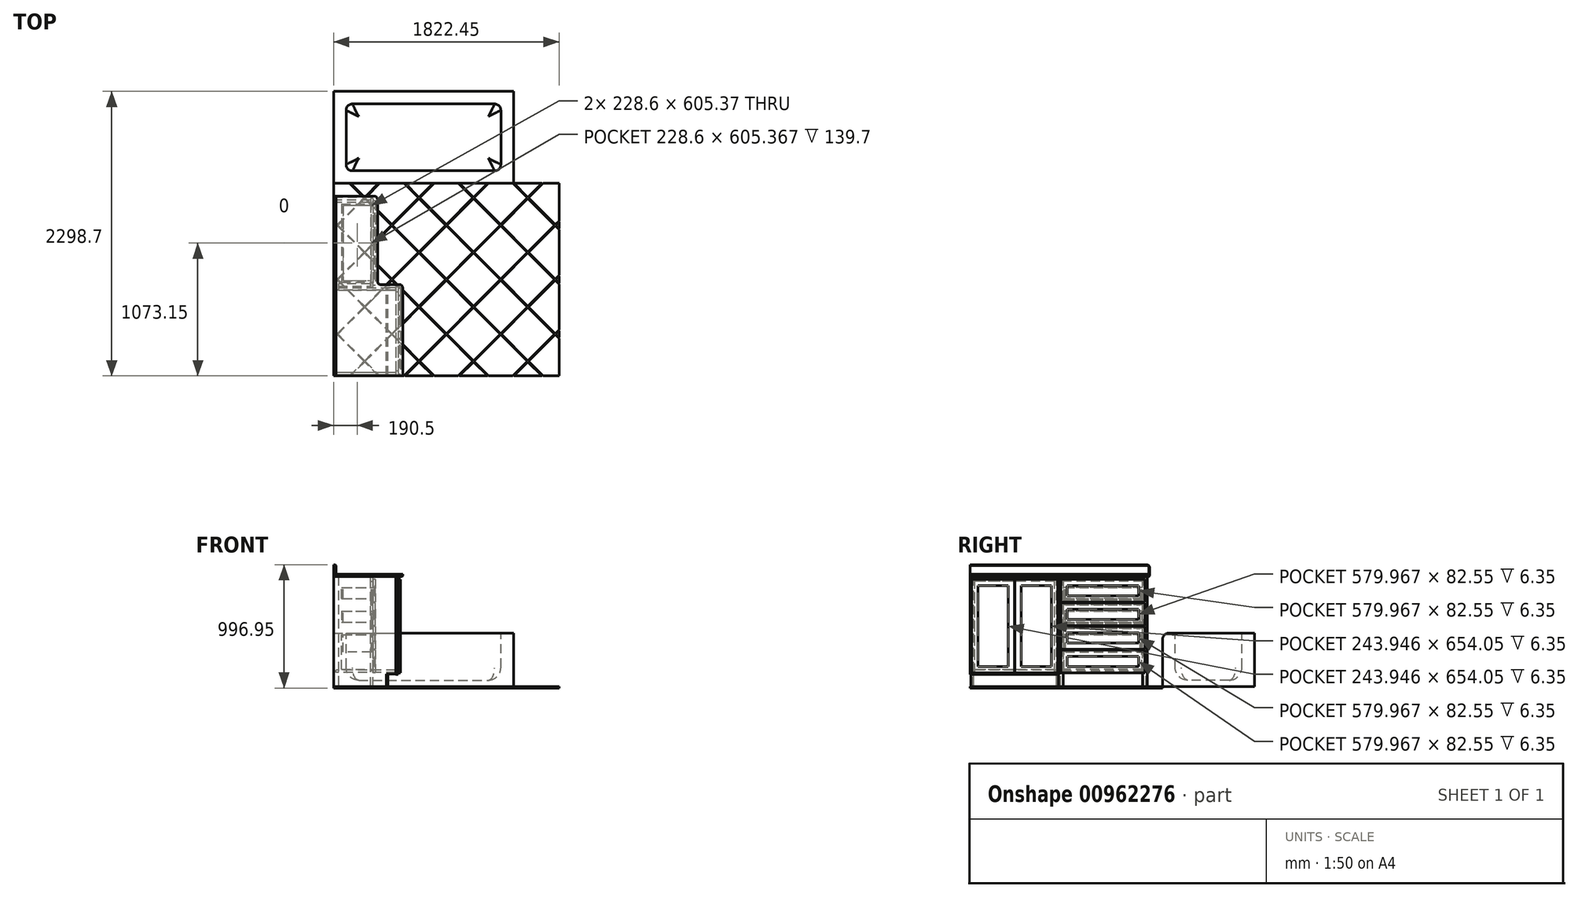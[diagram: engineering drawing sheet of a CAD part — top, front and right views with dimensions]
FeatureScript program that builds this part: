
annotation { "Feature Type Name" : "Feature", "Feature Type Description" : "" }
export const myFeature = defineFeature(function(context is Context, id is Id, definition is map)
    precondition{}
    {
        {
            var Q0;
            Q0=qCreatedBy(makeId("Top.planeOp"),FACE);
            var sketch = newSketch(context, id + "F0", { "sketchPlane" : qUnion([Q0])});
            skLineSegment(sketch, "E0", {"start": v(863.6, 0) * mm, "end": v(1631.95, 0) * mm});
            skLineSegment(sketch, "E1", {"start": v(863.6, 0) * mm, "end": v(0, 0) * mm});
            skLineSegment(sketch, "E2", {"start": v(0, 0) * mm, "end": v(0, 2298.7) * mm});
            skLineSegment(sketch, "E3", {"start": v(0, 2298.7) * mm, "end": v(1454.15, 2298.7) * mm});
            skLineSegment(sketch, "E4", {"start": v(1454.15, 2298.7) * mm, "end": v(1454.15, 1555.75) * mm});
            skLineSegment(sketch, "E5", {"start": v(1454.15, 1555.75) * mm, "end": v(1822.45, 1555.75) * mm});
            skLineSegment(sketch, "E6", {"start": v(1822.45, 1555.75) * mm, "end": v(1822.45, 0) * mm});
            skLineSegment(sketch, "E7", {"start": v(1822.45, 0) * mm, "end": v(1631.95, 0) * mm});
            skLineSegment(sketch, "E8", {"start": v(1454.15, 1555.75) * mm, "end": v(0, 1555.75) * mm, "construction": true});
            skLineSegment(sketch, "E9", {"start": v(1466.85, 1327.15) * mm, "end": v(1466.85, 819.15) * mm, "construction": true});
            skLineSegment(sketch, "E10", {"start": v(1111.25, 1073.15) * mm, "end": v(1822.45, 1073.15) * mm, "construction": true});
            skPoint(sketch, "E11", {"position": v(1466.85, 1073.15) * mm});
            skEllipse(sketch, "E12", {"center": v(1466.85, 1073.15) * mm, "majorRadius": 355.6 * mm, "minorRadius": 254 * mm, "majorAxis": v(1, 0)});
            skSolve(sketch);
        }
        {
            var Q0;
            Q0=qCreatedBy(makeId("Top.planeOp"),FACE);
            var sketch = newSketch(context, id + "F1", { "sketchPlane" : qUnion([Q0])});
            skLineSegment(sketch, "E13", {"start": v(863.6, 0) * mm, "end": v(1631.95, 0) * mm});
            skLineSegment(sketch, "E14", {"start": v(863.6, 0) * mm, "end": v(0, 0) * mm});
            skLineSegment(sketch, "E15", {"start": v(0, 0) * mm, "end": v(0, 2298.7) * mm});
            skLineSegment(sketch, "E16", {"start": v(0, 2298.7) * mm, "end": v(1454.15, 2298.7) * mm});
            skLineSegment(sketch, "E17", {"start": v(1454.15, 2298.7) * mm, "end": v(1454.15, 1555.75) * mm});
            skLineSegment(sketch, "E18", {"start": v(1454.15, 1555.75) * mm, "end": v(1822.45, 1555.75) * mm});
            skLineSegment(sketch, "E19", {"start": v(1822.45, 1555.75) * mm, "end": v(1822.45, 0) * mm});
            skLineSegment(sketch, "E20", {"start": v(1822.45, 0) * mm, "end": v(1631.95, 0) * mm});
            skLineSegment(sketch, "E21", {"start": v(1454.15, 1555.75) * mm, "end": v(0, 1555.75) * mm, "construction": true});
            skLineSegment(sketch, "E22", {"start": v(1466.85, 1327.15) * mm, "end": v(1466.85, 819.15) * mm, "construction": true});
            skLineSegment(sketch, "E23", {"start": v(1111.25, 1073.15) * mm, "end": v(1822.45, 1073.15) * mm, "construction": true});
            skPoint(sketch, "E24", {"position": v(1466.85, 1073.15) * mm});
            skEllipse(sketch, "E25", {"center": v(1466.85, 1073.15) * mm, "majorRadius": 355.6 * mm, "minorRadius": 254 * mm, "majorAxis": v(1, 0)});
            skEllipse(sketch, "E26", {"center": v(330.2, 508) * mm, "majorRadius": 336.55 * mm, "minorRadius": 228.6 * mm, "majorAxis": v(0, -1)});
            skLineSegment(sketch, "E27", {"start": v(330.2, 844.55) * mm, "end": v(330.2, 171.45) * mm, "construction": true});
            skLineSegment(sketch, "E28", {"start": v(558.8, 508) * mm, "end": v(101.6, 508) * mm, "construction": true});
            skLineSegment(sketch, "E29", {"start": v(101.6, 508) * mm, "end": v(0, 508) * mm, "construction": true});
            skLineSegment(sketch, "E30.bottom", {"start": v(63.5, 1403.35) * mm, "end": v(431.8, 1403.35) * mm});
            skLineSegment(sketch, "E30.top", {"start": v(63.5, 996.95) * mm, "end": v(431.8, 996.95) * mm});
            skLineSegment(sketch, "E30.left", {"start": v(63.5, 1403.35) * mm, "end": v(63.5, 996.95) * mm});
            skLineSegment(sketch, "E30.right", {"start": v(431.8, 1403.35) * mm, "end": v(431.8, 996.95) * mm});
            skLineSegment(sketch, "E31", {"start": v(0, 787.4) * mm, "end": v(302.35, 842.04) * mm});
            skLineSegment(sketch, "E32", {"start": v(0, 228.6) * mm, "end": v(302.35, 173.96) * mm});
            skSolve(sketch);
        }
        {
            var Q0;
            Q0=qCreatedBy(makeId("Top.planeOp"),FACE);
            var sketch = newSketch(context, id + "F2", { "sketchPlane" : qUnion([Q0])});
            skLineSegment(sketch, "E33.bottom", {"start": v(520.7, 0) * mm, "end": v(501.65, 0) * mm});
            skLineSegment(sketch, "E33.top", {"start": v(520.7, 38.1) * mm, "end": v(501.65, 38.1) * mm});
            skLineSegment(sketch, "E33.left", {"start": v(520.7, 0) * mm, "end": v(520.7, 38.1) * mm});
            skLineSegment(sketch, "E33.right", {"start": v(501.65, 0) * mm, "end": v(501.65, 38.1) * mm});
            skLineSegment(sketch, "E34.bottom", {"start": v(520.7, 681.57) * mm, "end": v(501.65, 681.57) * mm});
            skLineSegment(sketch, "E34.top", {"start": v(520.7, 719.67) * mm, "end": v(501.65, 719.67) * mm});
            skLineSegment(sketch, "E34.left", {"start": v(520.7, 681.57) * mm, "end": v(520.7, 719.67) * mm});
            skLineSegment(sketch, "E34.right", {"start": v(501.65, 681.57) * mm, "end": v(501.65, 719.67) * mm});
            skLineSegment(sketch, "E35.bottom", {"start": v(317.5, 1394.88) * mm, "end": v(298.45, 1394.88) * mm});
            skLineSegment(sketch, "E35.top", {"start": v(317.5, 1432.98) * mm, "end": v(298.45, 1432.98) * mm});
            skLineSegment(sketch, "E35.left", {"start": v(317.5, 1394.88) * mm, "end": v(317.5, 1432.98) * mm});
            skLineSegment(sketch, "E35.right", {"start": v(298.45, 1394.88) * mm, "end": v(298.45, 1432.98) * mm});
            skLineSegment(sketch, "E36", {"start": v(317.5, 1394.88) * mm, "end": v(317.5, 751.42) * mm});
            skLineSegment(sketch, "E37", {"start": v(298.45, 1394.88) * mm, "end": v(298.45, 751.42) * mm});
            skLineSegment(sketch, "E38.bottom", {"start": v(298.45, 751.42) * mm, "end": v(317.5, 751.42) * mm});
            skLineSegment(sketch, "E38.top", {"start": v(298.45, 713.32) * mm, "end": v(317.5, 713.32) * mm});
            skLineSegment(sketch, "E38.left", {"start": v(298.45, 751.42) * mm, "end": v(298.45, 713.32) * mm});
            skLineSegment(sketch, "E38.right", {"start": v(317.5, 751.42) * mm, "end": v(317.5, 713.32) * mm});
            skLineSegment(sketch, "E39", {"start": v(501.65, 713.32) * mm, "end": v(38.1, 713.32) * mm});
            skLineSegment(sketch, "E40", {"start": v(501.65, 694.27) * mm, "end": v(38.1, 694.27) * mm});
            skLineSegment(sketch, "E41", {"start": v(501.65, 681.57) * mm, "end": v(501.65, 38.1) * mm});
            skLineSegment(sketch, "E42", {"start": v(520.7, 681.57) * mm, "end": v(520.7, 38.1) * mm});
            skLineSegment(sketch, "E43", {"start": v(298.45, 1420.28) * mm, "end": v(0, 1420.28) * mm});
            skLineSegment(sketch, "E44", {"start": v(0, 1420.28) * mm, "end": v(0, 1401.23) * mm});
            skLineSegment(sketch, "E45", {"start": v(0, 1401.23) * mm, "end": v(298.45, 1401.23) * mm});
            skLineSegment(sketch, "E46", {"start": v(0, 1420.28) * mm, "end": v(0, 1426.63) * mm});
            skLineSegment(sketch, "E47", {"start": v(0, 1426.63) * mm, "end": v(298.45, 1426.63) * mm});
            skLineSegment(sketch, "E48", {"start": v(501.65, 6.35) * mm, "end": v(0, 6.35) * mm});
            skLineSegment(sketch, "E49", {"start": v(0, 6.35) * mm, "end": v(0, 25.4) * mm});
            skLineSegment(sketch, "E50", {"start": v(0, 25.4) * mm, "end": v(501.65, 25.4) * mm});
            skLineSegment(sketch, "E51", {"start": v(38.1, 713.32) * mm, "end": v(38.1, 694.27) * mm});
            skLineSegment(sketch, "E52", {"start": v(298.45, 745.07) * mm, "end": v(38.1, 745.07) * mm});
            skLineSegment(sketch, "E53", {"start": v(38.1, 745.07) * mm, "end": v(38.1, 726.02) * mm});
            skLineSegment(sketch, "E54", {"start": v(38.1, 726.02) * mm, "end": v(298.45, 726.02) * mm});
            skLineSegment(sketch, "E55", {"start": v(0, 1394.88) * mm, "end": v(0, 31.75) * mm});
            skLineSegment(sketch, "E56", {"start": v(19.05, 1401.23) * mm, "end": v(19.05, 25.4) * mm});
            skLineSegment(sketch, "E57", {"start": v(38.1, 1401.23) * mm, "end": v(38.1, 25.4) * mm});
            skLineSegment(sketch, "E58", {"start": v(0, 1452.03) * mm, "end": v(355.6, 1452.03) * mm});
            skLineSegment(sketch, "E59", {"start": v(355.6, 1452.03) * mm, "end": v(355.6, 738.72) * mm});
            skLineSegment(sketch, "E60", {"start": v(355.6, 738.72) * mm, "end": v(558.8, 738.72) * mm});
            skLineSegment(sketch, "E61", {"start": v(558.8, 738.72) * mm, "end": v(558.8, 0) * mm});
            skLineSegment(sketch, "E62", {"start": v(558.8, 0) * mm, "end": v(0, 0) * mm});
            skLineSegment(sketch, "E63", {"start": v(0, 0) * mm, "end": v(0, 1452.03) * mm});
            skLineSegment(sketch, "E64", {"start": v(317.5, 1413.93) * mm, "end": v(336.55, 1413.93) * mm, "construction": true});
            skLineSegment(sketch, "E65", {"start": v(336.55, 1413.93) * mm, "end": v(336.55, 732.37) * mm, "construction": true});
            skLineSegment(sketch, "E66", {"start": v(336.55, 732.37) * mm, "end": v(317.5, 732.37) * mm, "construction": true});
            skLineSegment(sketch, "E67", {"start": v(317.5, 1388.53) * mm, "end": v(63.5, 1388.53) * mm, "construction": true});
            skLineSegment(sketch, "E68", {"start": v(63.5, 757.77) * mm, "end": v(317.5, 757.77) * mm, "construction": true});
            skLineSegment(sketch, "E69", {"start": v(63.5, 1388.53) * mm, "end": v(63.5, 1375.83) * mm, "construction": true});
            skLineSegment(sketch, "E70", {"start": v(63.5, 1375.83) * mm, "end": v(76.2, 1375.83) * mm, "construction": true});
            skLineSegment(sketch, "E71", {"start": v(76.2, 770.47) * mm, "end": v(63.5, 770.47) * mm, "construction": true});
            skLineSegment(sketch, "E72", {"start": v(63.5, 770.47) * mm, "end": v(63.5, 757.77) * mm, "construction": true});
            skLineSegment(sketch, "E73", {"start": v(76.2, 1382.18) * mm, "end": v(76.2, 764.12) * mm, "construction": true});
            skLineSegment(sketch, "E74", {"start": v(76.2, 764.12) * mm, "end": v(82.55, 764.12) * mm, "construction": true});
            skLineSegment(sketch, "E75", {"start": v(82.55, 764.12) * mm, "end": v(82.55, 770.47) * mm, "construction": true});
            skLineSegment(sketch, "E76", {"start": v(76.2, 1382.18) * mm, "end": v(82.55, 1382.18) * mm, "construction": true});
            skLineSegment(sketch, "E77", {"start": v(82.55, 1382.18) * mm, "end": v(82.55, 1375.83) * mm, "construction": true});
            skLineSegment(sketch, "E78", {"start": v(88.9, 1375.83) * mm, "end": v(88.9, 770.47) * mm, "construction": true});
            skLineSegment(sketch, "E79", {"start": v(82.55, 1375.83) * mm, "end": v(317.5, 1375.83) * mm, "construction": true});
            skLineSegment(sketch, "E80", {"start": v(82.55, 770.47) * mm, "end": v(317.5, 770.47) * mm, "construction": true});
            skLineSegment(sketch, "E81", {"start": v(317.5, 1073.15) * mm, "end": v(336.55, 1073.15) * mm, "construction": true});
            skLineSegment(sketch, "E82", {"start": v(520.7, 706.97) * mm, "end": v(539.75, 706.97) * mm, "construction": true});
            skLineSegment(sketch, "E83", {"start": v(539.75, 706.97) * mm, "end": v(539.75, 361.42) * mm, "construction": true});
            skLineSegment(sketch, "E84", {"start": v(539.75, 361.42) * mm, "end": v(520.7, 361.42) * mm, "construction": true});
            skLineSegment(sketch, "E85", {"start": v(520.7, 358.25) * mm, "end": v(539.75, 358.25) * mm, "construction": true});
            skLineSegment(sketch, "E86", {"start": v(539.75, 358.25) * mm, "end": v(539.75, 12.7) * mm, "construction": true});
            skLineSegment(sketch, "E87", {"start": v(539.75, 12.7) * mm, "end": v(520.7, 12.7) * mm, "construction": true});
            skLineSegment(sketch, "E88", {"start": v(539.75, 361.42) * mm, "end": v(539.75, 358.25) * mm, "construction": true});
            skLineSegment(sketch, "E89", {"start": v(539.75, 359.83) * mm, "end": v(520.7, 359.83) * mm, "construction": true});
            skLineSegment(sketch, "E90", {"start": v(0, 1394.88) * mm, "end": v(19.05, 1394.88) * mm});
            skLineSegment(sketch, "E91", {"start": v(0, 31.75) * mm, "end": v(19.05, 31.75) * mm});
            skLineSegment(sketch, "E92", {"start": v(76.2, 668.87) * mm, "end": v(76.2, 50.8) * mm, "construction": true});
            skLineSegment(sketch, "E93", {"start": v(63.5, 57.15) * mm, "end": v(63.5, 44.45) * mm, "construction": true});
            skLineSegment(sketch, "E94", {"start": v(63.5, 44.45) * mm, "end": v(539.75, 44.45) * mm, "construction": true});
            skLineSegment(sketch, "E95", {"start": v(76.2, 50.8) * mm, "end": v(82.55, 50.8) * mm, "construction": true});
            skLineSegment(sketch, "E96", {"start": v(82.55, 50.8) * mm, "end": v(82.55, 57.15) * mm, "construction": true});
            skLineSegment(sketch, "E97", {"start": v(88.9, 57.15) * mm, "end": v(88.9, 662.52) * mm, "construction": true});
            skLineSegment(sketch, "E98", {"start": v(82.55, 662.52) * mm, "end": v(82.55, 668.87) * mm, "construction": true});
            skLineSegment(sketch, "E99", {"start": v(82.55, 668.87) * mm, "end": v(76.2, 668.87) * mm, "construction": true});
            skLineSegment(sketch, "E100", {"start": v(76.2, 662.52) * mm, "end": v(63.5, 662.52) * mm, "construction": true});
            skLineSegment(sketch, "E101", {"start": v(63.5, 662.52) * mm, "end": v(63.5, 675.22) * mm, "construction": true});
            skLineSegment(sketch, "E102", {"start": v(63.5, 675.22) * mm, "end": v(539.75, 675.22) * mm, "construction": true});
            skLineSegment(sketch, "E103", {"start": v(82.55, 662.52) * mm, "end": v(539.75, 662.52) * mm, "construction": true});
            skLineSegment(sketch, "E104", {"start": v(63.5, 57.15) * mm, "end": v(76.2, 57.15) * mm, "construction": true});
            skLineSegment(sketch, "E105", {"start": v(82.55, 57.15) * mm, "end": v(539.75, 57.15) * mm, "construction": true});
            skLineSegment(sketch, "E106", {"start": v(1466.85, 1073.15) * mm, "end": v(336.55, 1073.15) * mm, "construction": true});
            skSolve(sketch);
        }
        {
            var Q0;
            Q0=qCreatedBy(makeId("Top.planeOp"),FACE);
            var sketch = newSketch(context, id + "F3", { "sketchPlane" : qUnion([Q0])});
            skLineSegment(sketch, "E107", {"start": v(695.7, -762.24) * mm, "end": v(911.23, -977.77) * mm});
            skLineSegment(sketch, "E108", {"start": v(911.23, -977.77) * mm, "end": v(1126.75, -762.24) * mm});
            skLineSegment(sketch, "E109", {"start": v(1126.75, -762.24) * mm, "end": v(911.23, -546.71) * mm});
            skLineSegment(sketch, "E110", {"start": v(911.23, -546.71) * mm, "end": v(695.7, -762.24) * mm});
            skLineSegment(sketch, "E111.0.1.0", {"start": v(475.68, -542.22) * mm, "end": v(691.2, -757.75) * mm});
            skLineSegment(sketch, "E111.0.1.1", {"start": v(906.73, -542.22) * mm, "end": v(691.2, -326.7) * mm});
            skLineSegment(sketch, "E111.0.1.2", {"start": v(691.2, -326.7) * mm, "end": v(475.68, -542.22) * mm});
            skLineSegment(sketch, "E111.0.1.3", {"start": v(691.2, -757.75) * mm, "end": v(906.73, -542.22) * mm});
            skLineSegment(sketch, "E111.1.0.0", {"start": v(915.72, -542.22) * mm, "end": v(1131.24, -757.75) * mm});
            skLineSegment(sketch, "E111.1.0.1", {"start": v(1346.77, -542.22) * mm, "end": v(1131.24, -326.7) * mm});
            skLineSegment(sketch, "E111.1.0.2", {"start": v(1131.24, -326.7) * mm, "end": v(915.72, -542.22) * mm});
            skLineSegment(sketch, "E111.1.0.3", {"start": v(1131.24, -757.75) * mm, "end": v(1346.77, -542.22) * mm});
            skLineSegment(sketch, "E111.1.1.0", {"start": v(695.7, -322.2) * mm, "end": v(911.23, -537.73) * mm});
            skLineSegment(sketch, "E111.1.1.1", {"start": v(1126.75, -322.2) * mm, "end": v(911.23, -106.68) * mm});
            skLineSegment(sketch, "E111.1.1.2", {"start": v(911.23, -106.68) * mm, "end": v(695.7, -322.2) * mm});
            skLineSegment(sketch, "E111.1.1.3", {"start": v(911.23, -537.73) * mm, "end": v(1126.75, -322.2) * mm});
            skLineSegment(sketch, "E111.2.0.0", {"start": v(1135.73, -322.2) * mm, "end": v(1351.26, -537.73) * mm});
            skLineSegment(sketch, "E111.2.0.1", {"start": v(1566.78, -322.2) * mm, "end": v(1351.26, -106.68) * mm});
            skLineSegment(sketch, "E111.2.0.2", {"start": v(1351.26, -106.68) * mm, "end": v(1135.73, -322.2) * mm});
            skLineSegment(sketch, "E111.2.0.3", {"start": v(1351.26, -537.73) * mm, "end": v(1566.78, -322.2) * mm});
            skLineSegment(sketch, "E111.2.1.0", {"start": v(915.72, -102.2) * mm, "end": v(1131.24, -317.72) * mm});
            skLineSegment(sketch, "E111.2.1.1", {"start": v(1346.77, -102.2) * mm, "end": v(1131.24, 113.34) * mm});
            skLineSegment(sketch, "E111.2.1.2", {"start": v(1131.24, 113.34) * mm, "end": v(915.72, -102.2) * mm});
            skLineSegment(sketch, "E111.2.1.3", {"start": v(1131.24, -317.72) * mm, "end": v(1346.77, -102.2) * mm});
            skLineSegment(sketch, "E111.direction1", {"start": v(911.22, -977.77) * mm, "end": v(1131.24, -757.75) * mm, "construction": true});
            skLineSegment(sketch, "E111.direction2", {"start": v(911.23, -977.77) * mm, "end": v(691.2, -757.75) * mm, "construction": true});
            skLineSegment(sketch, "E112.0.3.0", {"start": v(1355.75, -102.2) * mm, "end": v(1571.27, -317.72) * mm});
            skLineSegment(sketch, "E112.3.3.0", {"start": v(1786.8, -102.2) * mm, "end": v(1571.27, 113.34) * mm});
            skLineSegment(sketch, "E112.6.3.0", {"start": v(1571.27, 113.34) * mm, "end": v(1355.75, -102.2) * mm});
            skLineSegment(sketch, "E112.9.3.0", {"start": v(1571.27, -317.72) * mm, "end": v(1786.8, -102.2) * mm});
            skLineSegment(sketch, "E112.0.3.1", {"start": v(1135.73, 117.83) * mm, "end": v(1351.26, -97.7) * mm});
            skLineSegment(sketch, "E112.3.3.1", {"start": v(1566.78, 117.83) * mm, "end": v(1351.26, 333.35) * mm});
            skLineSegment(sketch, "E112.6.3.1", {"start": v(1351.26, 333.35) * mm, "end": v(1135.73, 117.83) * mm});
            skLineSegment(sketch, "E112.9.3.1", {"start": v(1351.26, -97.7) * mm, "end": v(1566.78, 117.83) * mm});
            skLineSegment(sketch, "E112.0.4.0", {"start": v(1575.76, 117.83) * mm, "end": v(1791.3, -97.7) * mm});
            skLineSegment(sketch, "E112.3.4.0", {"start": v(2006.82, 117.83) * mm, "end": v(1791.3, 333.35) * mm});
            skLineSegment(sketch, "E112.6.4.0", {"start": v(1791.3, 333.35) * mm, "end": v(1575.76, 117.83) * mm});
            skLineSegment(sketch, "E112.9.4.0", {"start": v(1791.3, -97.7) * mm, "end": v(2006.82, 117.83) * mm});
            skLineSegment(sketch, "E112.0.4.1", {"start": v(1355.75, 337.84) * mm, "end": v(1571.27, 122.32) * mm});
            skLineSegment(sketch, "E112.3.4.1", {"start": v(1786.8, 337.84) * mm, "end": v(1571.27, 553.37) * mm});
            skLineSegment(sketch, "E112.6.4.1", {"start": v(1571.27, 553.37) * mm, "end": v(1355.75, 337.84) * mm});
            skLineSegment(sketch, "E112.9.4.1", {"start": v(1571.27, 122.32) * mm, "end": v(1786.8, 337.84) * mm});
            skLineSegment(sketch, "E113.0.0.2", {"start": v(255.67, -322.2) * mm, "end": v(471.2, -537.73) * mm});
            skLineSegment(sketch, "E113.3.0.2", {"start": v(686.72, -322.2) * mm, "end": v(471.2, -106.68) * mm});
            skLineSegment(sketch, "E113.6.0.2", {"start": v(471.2, -106.68) * mm, "end": v(255.67, -322.2) * mm});
            skLineSegment(sketch, "E113.9.0.2", {"start": v(471.2, -537.73) * mm, "end": v(686.72, -322.2) * mm});
            skLineSegment(sketch, "E113.0.0.3", {"start": v(35.65, -102.2) * mm, "end": v(251.18, -317.72) * mm});
            skLineSegment(sketch, "E113.3.0.3", {"start": v(466.7, -102.2) * mm, "end": v(251.18, 113.34) * mm});
            skLineSegment(sketch, "E113.6.0.3", {"start": v(251.18, 113.34) * mm, "end": v(35.65, -102.2) * mm});
            skLineSegment(sketch, "E113.9.0.3", {"start": v(251.18, -317.72) * mm, "end": v(466.7, -102.2) * mm});
            skLineSegment(sketch, "E113.0.0.4", {"start": v(-184.37, 117.83) * mm, "end": v(31.16, -97.7) * mm});
            skLineSegment(sketch, "E113.3.0.4", {"start": v(246.69, 117.83) * mm, "end": v(31.16, 333.35) * mm});
            skLineSegment(sketch, "E113.6.0.4", {"start": v(31.16, 333.35) * mm, "end": v(-184.37, 117.83) * mm});
            skLineSegment(sketch, "E113.9.0.4", {"start": v(31.16, -97.7) * mm, "end": v(246.69, 117.83) * mm});
            skLineSegment(sketch, "E113.0.1.2", {"start": v(475.68, -102.2) * mm, "end": v(691.2, -317.72) * mm});
            skLineSegment(sketch, "E113.3.1.2", {"start": v(906.73, -102.2) * mm, "end": v(691.2, 113.34) * mm});
            skLineSegment(sketch, "E113.6.1.2", {"start": v(691.2, 113.34) * mm, "end": v(475.68, -102.2) * mm});
            skLineSegment(sketch, "E113.9.1.2", {"start": v(691.2, -317.72) * mm, "end": v(906.73, -102.2) * mm});
            skLineSegment(sketch, "E113.0.1.3", {"start": v(255.67, 117.83) * mm, "end": v(471.2, -97.7) * mm});
            skLineSegment(sketch, "E113.3.1.3", {"start": v(686.72, 117.83) * mm, "end": v(471.2, 333.35) * mm});
            skLineSegment(sketch, "E113.6.1.3", {"start": v(471.2, 333.35) * mm, "end": v(255.67, 117.83) * mm});
            skLineSegment(sketch, "E113.9.1.3", {"start": v(471.2, -97.7) * mm, "end": v(686.72, 117.83) * mm});
            skLineSegment(sketch, "E113.0.1.4", {"start": v(35.65, 337.84) * mm, "end": v(251.18, 122.32) * mm});
            skLineSegment(sketch, "E113.3.1.4", {"start": v(466.7, 337.84) * mm, "end": v(251.18, 553.37) * mm});
            skLineSegment(sketch, "E113.6.1.4", {"start": v(251.18, 553.37) * mm, "end": v(35.65, 337.84) * mm});
            skLineSegment(sketch, "E113.9.1.4", {"start": v(251.18, 122.32) * mm, "end": v(466.7, 337.84) * mm});
            skLineSegment(sketch, "E113.0.2.2", {"start": v(695.7, 117.83) * mm, "end": v(911.23, -97.7) * mm});
            skLineSegment(sketch, "E113.3.2.2", {"start": v(1126.75, 117.83) * mm, "end": v(911.23, 333.35) * mm});
            skLineSegment(sketch, "E113.6.2.2", {"start": v(911.23, 333.35) * mm, "end": v(695.7, 117.83) * mm});
            skLineSegment(sketch, "E113.9.2.2", {"start": v(911.23, -97.7) * mm, "end": v(1126.75, 117.83) * mm});
            skLineSegment(sketch, "E113.0.2.3", {"start": v(475.68, 337.84) * mm, "end": v(691.2, 122.32) * mm});
            skLineSegment(sketch, "E113.3.2.3", {"start": v(906.73, 337.84) * mm, "end": v(691.2, 553.37) * mm});
            skLineSegment(sketch, "E113.6.2.3", {"start": v(691.2, 553.37) * mm, "end": v(475.68, 337.84) * mm});
            skLineSegment(sketch, "E113.9.2.3", {"start": v(691.2, 122.32) * mm, "end": v(906.73, 337.84) * mm});
            skLineSegment(sketch, "E113.0.2.4", {"start": v(255.67, 557.86) * mm, "end": v(471.2, 342.33) * mm});
            skLineSegment(sketch, "E113.3.2.4", {"start": v(686.72, 557.86) * mm, "end": v(471.2, 773.38) * mm});
            skLineSegment(sketch, "E113.6.2.4", {"start": v(471.2, 773.38) * mm, "end": v(255.67, 557.86) * mm});
            skLineSegment(sketch, "E113.9.2.4", {"start": v(471.2, 342.33) * mm, "end": v(686.72, 557.86) * mm});
            skLineSegment(sketch, "E113.0.3.2", {"start": v(915.72, 337.84) * mm, "end": v(1131.24, 122.32) * mm});
            skLineSegment(sketch, "E113.3.3.2", {"start": v(1346.77, 337.84) * mm, "end": v(1131.24, 553.37) * mm});
            skLineSegment(sketch, "E113.6.3.2", {"start": v(1131.24, 553.37) * mm, "end": v(915.72, 337.84) * mm});
            skLineSegment(sketch, "E113.9.3.2", {"start": v(1131.24, 122.32) * mm, "end": v(1346.77, 337.84) * mm});
            skLineSegment(sketch, "E113.0.3.3", {"start": v(695.7, 557.86) * mm, "end": v(911.23, 342.33) * mm});
            skLineSegment(sketch, "E113.3.3.3", {"start": v(1126.75, 557.86) * mm, "end": v(911.23, 773.38) * mm});
            skLineSegment(sketch, "E113.6.3.3", {"start": v(911.22, 773.38) * mm, "end": v(695.7, 557.86) * mm});
            skLineSegment(sketch, "E113.9.3.3", {"start": v(911.23, 342.33) * mm, "end": v(1126.75, 557.86) * mm});
            skLineSegment(sketch, "E113.0.3.4", {"start": v(475.68, 777.88) * mm, "end": v(691.2, 562.35) * mm});
            skLineSegment(sketch, "E113.3.3.4", {"start": v(906.73, 777.88) * mm, "end": v(691.2, 993.4) * mm});
            skLineSegment(sketch, "E113.6.3.4", {"start": v(691.2, 993.4) * mm, "end": v(475.68, 777.88) * mm});
            skLineSegment(sketch, "E113.9.3.4", {"start": v(691.2, 562.35) * mm, "end": v(906.73, 777.88) * mm});
            skLineSegment(sketch, "E113.0.4.2", {"start": v(1135.73, 557.86) * mm, "end": v(1351.26, 342.33) * mm});
            skLineSegment(sketch, "E113.3.4.2", {"start": v(1566.78, 557.86) * mm, "end": v(1351.26, 773.38) * mm});
            skLineSegment(sketch, "E113.6.4.2", {"start": v(1351.26, 773.38) * mm, "end": v(1135.73, 557.86) * mm});
            skLineSegment(sketch, "E113.9.4.2", {"start": v(1351.26, 342.33) * mm, "end": v(1566.78, 557.86) * mm});
            skLineSegment(sketch, "E113.0.4.3", {"start": v(915.72, 777.88) * mm, "end": v(1131.24, 562.35) * mm});
            skLineSegment(sketch, "E113.3.4.3", {"start": v(1346.77, 777.88) * mm, "end": v(1131.24, 993.4) * mm});
            skLineSegment(sketch, "E113.6.4.3", {"start": v(1131.24, 993.4) * mm, "end": v(915.72, 777.88) * mm});
            skLineSegment(sketch, "E113.9.4.3", {"start": v(1131.24, 562.35) * mm, "end": v(1346.77, 777.88) * mm});
            skLineSegment(sketch, "E113.0.4.4", {"start": v(695.7, 997.9) * mm, "end": v(911.23, 782.37) * mm});
            skLineSegment(sketch, "E113.3.4.4", {"start": v(1126.75, 997.9) * mm, "end": v(911.23, 1213.42) * mm});
            skLineSegment(sketch, "E113.6.4.4", {"start": v(911.22, 1213.42) * mm, "end": v(695.7, 997.9) * mm});
            skLineSegment(sketch, "E113.9.4.4", {"start": v(911.22, 782.37) * mm, "end": v(1126.75, 997.9) * mm});
            skLineSegment(sketch, "E114.0.5.0", {"start": v(1795.78, 337.84) * mm, "end": v(2011.3, 122.32) * mm});
            skLineSegment(sketch, "E114.3.5.0", {"start": v(2226.83, 337.84) * mm, "end": v(2011.3, 553.37) * mm});
            skLineSegment(sketch, "E114.6.5.0", {"start": v(2011.3, 553.37) * mm, "end": v(1795.78, 337.84) * mm});
            skLineSegment(sketch, "E114.9.5.0", {"start": v(2011.3, 122.32) * mm, "end": v(2226.83, 337.84) * mm});
            skLineSegment(sketch, "E114.0.5.1", {"start": v(1575.76, 557.86) * mm, "end": v(1791.3, 342.33) * mm});
            skLineSegment(sketch, "E114.3.5.1", {"start": v(2006.82, 557.86) * mm, "end": v(1791.3, 773.38) * mm});
            skLineSegment(sketch, "E114.6.5.1", {"start": v(1791.3, 773.38) * mm, "end": v(1575.76, 557.86) * mm});
            skLineSegment(sketch, "E114.9.5.1", {"start": v(1791.3, 342.33) * mm, "end": v(2006.82, 557.86) * mm});
            skLineSegment(sketch, "E114.0.5.2", {"start": v(1355.75, 777.88) * mm, "end": v(1571.27, 562.35) * mm});
            skLineSegment(sketch, "E114.3.5.2", {"start": v(1786.8, 777.88) * mm, "end": v(1571.27, 993.4) * mm});
            skLineSegment(sketch, "E114.6.5.2", {"start": v(1571.27, 993.4) * mm, "end": v(1355.75, 777.88) * mm});
            skLineSegment(sketch, "E114.9.5.2", {"start": v(1571.27, 562.35) * mm, "end": v(1786.8, 777.88) * mm});
            skLineSegment(sketch, "E114.0.5.3", {"start": v(1135.73, 997.9) * mm, "end": v(1351.26, 782.37) * mm});
            skLineSegment(sketch, "E114.3.5.3", {"start": v(1566.78, 997.9) * mm, "end": v(1351.26, 1213.42) * mm});
            skLineSegment(sketch, "E114.6.5.3", {"start": v(1351.26, 1213.42) * mm, "end": v(1135.73, 997.9) * mm});
            skLineSegment(sketch, "E114.9.5.3", {"start": v(1351.26, 782.37) * mm, "end": v(1566.78, 997.9) * mm});
            skLineSegment(sketch, "E114.0.5.4", {"start": v(915.72, 1217.9) * mm, "end": v(1131.24, 1002.38) * mm});
            skLineSegment(sketch, "E114.3.5.4", {"start": v(1346.77, 1217.9) * mm, "end": v(1131.24, 1433.43) * mm});
            skLineSegment(sketch, "E114.6.5.4", {"start": v(1131.24, 1433.43) * mm, "end": v(915.72, 1217.9) * mm});
            skLineSegment(sketch, "E114.9.5.4", {"start": v(1131.24, 1002.38) * mm, "end": v(1346.77, 1217.9) * mm});
            skLineSegment(sketch, "E114.0.6.0", {"start": v(2015.8, 557.86) * mm, "end": v(2231.32, 342.33) * mm});
            skLineSegment(sketch, "E114.3.6.0", {"start": v(2446.85, 557.86) * mm, "end": v(2231.32, 773.38) * mm});
            skLineSegment(sketch, "E114.6.6.0", {"start": v(2231.32, 773.38) * mm, "end": v(2015.8, 557.86) * mm});
            skLineSegment(sketch, "E114.9.6.0", {"start": v(2231.32, 342.33) * mm, "end": v(2446.85, 557.86) * mm});
            skLineSegment(sketch, "E114.0.6.1", {"start": v(1795.78, 777.88) * mm, "end": v(2011.3, 562.35) * mm});
            skLineSegment(sketch, "E114.3.6.1", {"start": v(2226.83, 777.88) * mm, "end": v(2011.3, 993.4) * mm});
            skLineSegment(sketch, "E114.6.6.1", {"start": v(2011.3, 993.4) * mm, "end": v(1795.78, 777.88) * mm});
            skLineSegment(sketch, "E114.9.6.1", {"start": v(2011.3, 562.35) * mm, "end": v(2226.83, 777.88) * mm});
            skLineSegment(sketch, "E114.0.6.2", {"start": v(1575.76, 997.9) * mm, "end": v(1791.3, 782.37) * mm});
            skLineSegment(sketch, "E114.3.6.2", {"start": v(2006.82, 997.9) * mm, "end": v(1791.3, 1213.42) * mm});
            skLineSegment(sketch, "E114.6.6.2", {"start": v(1791.3, 1213.42) * mm, "end": v(1575.76, 997.9) * mm});
            skLineSegment(sketch, "E114.9.6.2", {"start": v(1791.3, 782.37) * mm, "end": v(2006.82, 997.9) * mm});
            skLineSegment(sketch, "E114.0.6.3", {"start": v(1355.75, 1217.9) * mm, "end": v(1571.27, 1002.38) * mm});
            skLineSegment(sketch, "E114.3.6.3", {"start": v(1786.8, 1217.9) * mm, "end": v(1571.27, 1433.43) * mm});
            skLineSegment(sketch, "E114.6.6.3", {"start": v(1571.27, 1433.43) * mm, "end": v(1355.75, 1217.9) * mm});
            skLineSegment(sketch, "E114.9.6.3", {"start": v(1571.27, 1002.38) * mm, "end": v(1786.8, 1217.9) * mm});
            skLineSegment(sketch, "E114.0.6.4", {"start": v(1135.73, 1437.92) * mm, "end": v(1351.26, 1222.4) * mm});
            skLineSegment(sketch, "E114.3.6.4", {"start": v(1566.78, 1437.92) * mm, "end": v(1351.26, 1653.45) * mm});
            skLineSegment(sketch, "E114.6.6.4", {"start": v(1351.26, 1653.45) * mm, "end": v(1135.73, 1437.92) * mm});
            skLineSegment(sketch, "E114.9.6.4", {"start": v(1351.26, 1222.4) * mm, "end": v(1566.78, 1437.92) * mm});
            skLineSegment(sketch, "E115.0.0.5", {"start": v(-404.38, 337.84) * mm, "end": v(-188.86, 122.32) * mm});
            skLineSegment(sketch, "E115.3.0.5", {"start": v(26.67, 337.84) * mm, "end": v(-188.86, 553.37) * mm});
            skLineSegment(sketch, "E115.6.0.5", {"start": v(-188.86, 553.37) * mm, "end": v(-404.38, 337.84) * mm});
            skLineSegment(sketch, "E115.9.0.5", {"start": v(-188.86, 122.32) * mm, "end": v(26.67, 337.84) * mm});
            skLineSegment(sketch, "E115.0.0.6", {"start": v(-624.4, 557.86) * mm, "end": v(-408.87, 342.33) * mm});
            skLineSegment(sketch, "E115.3.0.6", {"start": v(-193.35, 557.86) * mm, "end": v(-408.87, 773.38) * mm});
            skLineSegment(sketch, "E115.6.0.6", {"start": v(-408.87, 773.38) * mm, "end": v(-624.4, 557.86) * mm});
            skLineSegment(sketch, "E115.9.0.6", {"start": v(-408.87, 342.33) * mm, "end": v(-193.35, 557.86) * mm});
            skLineSegment(sketch, "E115.0.1.5", {"start": v(-184.37, 557.86) * mm, "end": v(31.16, 342.33) * mm});
            skLineSegment(sketch, "E115.3.1.5", {"start": v(246.69, 557.86) * mm, "end": v(31.16, 773.38) * mm});
            skLineSegment(sketch, "E115.6.1.5", {"start": v(31.16, 773.38) * mm, "end": v(-184.37, 557.86) * mm});
            skLineSegment(sketch, "E115.9.1.5", {"start": v(31.16, 342.33) * mm, "end": v(246.69, 557.86) * mm});
            skLineSegment(sketch, "E115.0.1.6", {"start": v(-404.38, 777.88) * mm, "end": v(-188.86, 562.35) * mm});
            skLineSegment(sketch, "E115.3.1.6", {"start": v(26.67, 777.88) * mm, "end": v(-188.86, 993.4) * mm});
            skLineSegment(sketch, "E115.6.1.6", {"start": v(-188.86, 993.4) * mm, "end": v(-404.38, 777.88) * mm});
            skLineSegment(sketch, "E115.9.1.6", {"start": v(-188.86, 562.35) * mm, "end": v(26.67, 777.88) * mm});
            skLineSegment(sketch, "E115.0.2.5", {"start": v(35.65, 777.88) * mm, "end": v(251.18, 562.35) * mm});
            skLineSegment(sketch, "E115.3.2.5", {"start": v(466.7, 777.88) * mm, "end": v(251.18, 993.4) * mm});
            skLineSegment(sketch, "E115.6.2.5", {"start": v(251.18, 993.4) * mm, "end": v(35.65, 777.88) * mm});
            skLineSegment(sketch, "E115.9.2.5", {"start": v(251.18, 562.35) * mm, "end": v(466.7, 777.88) * mm});
            skLineSegment(sketch, "E115.0.2.6", {"start": v(-184.37, 997.9) * mm, "end": v(31.16, 782.37) * mm});
            skLineSegment(sketch, "E115.3.2.6", {"start": v(246.69, 997.9) * mm, "end": v(31.16, 1213.42) * mm});
            skLineSegment(sketch, "E115.6.2.6", {"start": v(31.16, 1213.42) * mm, "end": v(-184.37, 997.9) * mm});
            skLineSegment(sketch, "E115.9.2.6", {"start": v(31.16, 782.37) * mm, "end": v(246.69, 997.9) * mm});
            skLineSegment(sketch, "E115.0.3.5", {"start": v(255.67, 997.9) * mm, "end": v(471.2, 782.37) * mm});
            skLineSegment(sketch, "E115.3.3.5", {"start": v(686.72, 997.9) * mm, "end": v(471.2, 1213.42) * mm});
            skLineSegment(sketch, "E115.6.3.5", {"start": v(471.2, 1213.42) * mm, "end": v(255.67, 997.9) * mm});
            skLineSegment(sketch, "E115.9.3.5", {"start": v(471.2, 782.37) * mm, "end": v(686.72, 997.9) * mm});
            skLineSegment(sketch, "E115.0.3.6", {"start": v(35.65, 1217.9) * mm, "end": v(251.18, 1002.38) * mm});
            skLineSegment(sketch, "E115.3.3.6", {"start": v(466.7, 1217.9) * mm, "end": v(251.18, 1433.43) * mm});
            skLineSegment(sketch, "E115.6.3.6", {"start": v(251.18, 1433.43) * mm, "end": v(35.65, 1217.9) * mm});
            skLineSegment(sketch, "E115.9.3.6", {"start": v(251.18, 1002.38) * mm, "end": v(466.7, 1217.9) * mm});
            skLineSegment(sketch, "E115.0.4.5", {"start": v(475.68, 1217.9) * mm, "end": v(691.2, 1002.38) * mm});
            skLineSegment(sketch, "E115.3.4.5", {"start": v(906.73, 1217.9) * mm, "end": v(691.2, 1433.43) * mm});
            skLineSegment(sketch, "E115.6.4.5", {"start": v(691.2, 1433.43) * mm, "end": v(475.68, 1217.9) * mm});
            skLineSegment(sketch, "E115.9.4.5", {"start": v(691.2, 1002.38) * mm, "end": v(906.73, 1217.9) * mm});
            skLineSegment(sketch, "E115.0.4.6", {"start": v(255.67, 1437.92) * mm, "end": v(471.2, 1222.4) * mm});
            skLineSegment(sketch, "E115.3.4.6", {"start": v(686.72, 1437.92) * mm, "end": v(471.2, 1653.45) * mm});
            skLineSegment(sketch, "E115.6.4.6", {"start": v(471.2, 1653.45) * mm, "end": v(255.67, 1437.92) * mm});
            skLineSegment(sketch, "E115.9.4.6", {"start": v(471.2, 1222.4) * mm, "end": v(686.72, 1437.92) * mm});
            skLineSegment(sketch, "E115.0.5.5", {"start": v(695.7, 1437.92) * mm, "end": v(911.23, 1222.4) * mm});
            skLineSegment(sketch, "E115.3.5.5", {"start": v(1126.75, 1437.92) * mm, "end": v(911.22, 1653.45) * mm});
            skLineSegment(sketch, "E115.6.5.5", {"start": v(911.22, 1653.45) * mm, "end": v(695.7, 1437.92) * mm});
            skLineSegment(sketch, "E115.9.5.5", {"start": v(911.23, 1222.4) * mm, "end": v(1126.75, 1437.92) * mm});
            skLineSegment(sketch, "E115.0.5.6", {"start": v(475.68, 1657.94) * mm, "end": v(691.2, 1442.41) * mm});
            skLineSegment(sketch, "E115.3.5.6", {"start": v(906.73, 1657.94) * mm, "end": v(691.2, 1873.47) * mm});
            skLineSegment(sketch, "E115.6.5.6", {"start": v(691.2, 1873.47) * mm, "end": v(475.68, 1657.94) * mm});
            skLineSegment(sketch, "E115.9.5.6", {"start": v(691.2, 1442.41) * mm, "end": v(906.73, 1657.94) * mm});
            skLineSegment(sketch, "E115.0.6.5", {"start": v(915.72, 1657.94) * mm, "end": v(1131.24, 1442.41) * mm});
            skLineSegment(sketch, "E115.3.6.5", {"start": v(1346.77, 1657.94) * mm, "end": v(1131.24, 1873.47) * mm});
            skLineSegment(sketch, "E115.6.6.5", {"start": v(1131.24, 1873.47) * mm, "end": v(915.72, 1657.94) * mm});
            skLineSegment(sketch, "E115.9.6.5", {"start": v(1131.24, 1442.41) * mm, "end": v(1346.77, 1657.94) * mm});
            skLineSegment(sketch, "E115.0.6.6", {"start": v(695.7, 1877.96) * mm, "end": v(911.22, 1662.43) * mm});
            skLineSegment(sketch, "E115.3.6.6", {"start": v(1126.75, 1877.96) * mm, "end": v(911.22, 2093.48) * mm});
            skLineSegment(sketch, "E115.6.6.6", {"start": v(911.22, 2093.48) * mm, "end": v(695.7, 1877.96) * mm});
            skLineSegment(sketch, "E115.9.6.6", {"start": v(911.22, 1662.43) * mm, "end": v(1126.75, 1877.96) * mm});
            skLineSegment(sketch, "E116.0.0.7", {"start": v(-844.42, 777.88) * mm, "end": v(-628.89, 562.35) * mm});
            skLineSegment(sketch, "E116.3.0.7", {"start": v(-413.36, 777.88) * mm, "end": v(-628.89, 993.4) * mm});
            skLineSegment(sketch, "E116.6.0.7", {"start": v(-628.89, 993.4) * mm, "end": v(-844.42, 777.87) * mm});
            skLineSegment(sketch, "E116.9.0.7", {"start": v(-628.89, 562.35) * mm, "end": v(-413.36, 777.88) * mm});
            skLineSegment(sketch, "E116.0.1.7", {"start": v(-624.4, 997.9) * mm, "end": v(-408.87, 782.37) * mm});
            skLineSegment(sketch, "E116.3.1.7", {"start": v(-193.35, 997.9) * mm, "end": v(-408.87, 1213.42) * mm});
            skLineSegment(sketch, "E116.6.1.7", {"start": v(-408.87, 1213.42) * mm, "end": v(-624.4, 997.9) * mm});
            skLineSegment(sketch, "E116.9.1.7", {"start": v(-408.87, 782.37) * mm, "end": v(-193.35, 997.9) * mm});
            skLineSegment(sketch, "E116.0.2.7", {"start": v(-404.38, 1217.9) * mm, "end": v(-188.86, 1002.38) * mm});
            skLineSegment(sketch, "E116.3.2.7", {"start": v(26.67, 1217.9) * mm, "end": v(-188.86, 1433.43) * mm});
            skLineSegment(sketch, "E116.6.2.7", {"start": v(-188.86, 1433.43) * mm, "end": v(-404.38, 1217.9) * mm});
            skLineSegment(sketch, "E116.9.2.7", {"start": v(-188.86, 1002.38) * mm, "end": v(26.67, 1217.9) * mm});
            skLineSegment(sketch, "E116.0.3.7", {"start": v(-184.37, 1437.92) * mm, "end": v(31.16, 1222.4) * mm});
            skLineSegment(sketch, "E116.3.3.7", {"start": v(246.69, 1437.92) * mm, "end": v(31.16, 1653.45) * mm});
            skLineSegment(sketch, "E116.6.3.7", {"start": v(31.16, 1653.45) * mm, "end": v(-184.37, 1437.92) * mm});
            skLineSegment(sketch, "E116.9.3.7", {"start": v(31.16, 1222.4) * mm, "end": v(246.69, 1437.92) * mm});
            skLineSegment(sketch, "E116.0.4.7", {"start": v(35.65, 1657.94) * mm, "end": v(251.18, 1442.41) * mm});
            skLineSegment(sketch, "E116.3.4.7", {"start": v(466.7, 1657.94) * mm, "end": v(251.18, 1873.47) * mm});
            skLineSegment(sketch, "E116.6.4.7", {"start": v(251.18, 1873.47) * mm, "end": v(35.65, 1657.94) * mm});
            skLineSegment(sketch, "E116.9.4.7", {"start": v(251.18, 1442.41) * mm, "end": v(466.7, 1657.94) * mm});
            skLineSegment(sketch, "E116.0.5.7", {"start": v(255.67, 1877.96) * mm, "end": v(471.2, 1662.43) * mm});
            skLineSegment(sketch, "E116.3.5.7", {"start": v(686.72, 1877.96) * mm, "end": v(471.2, 2093.48) * mm});
            skLineSegment(sketch, "E116.6.5.7", {"start": v(471.2, 2093.48) * mm, "end": v(255.67, 1877.96) * mm});
            skLineSegment(sketch, "E116.9.5.7", {"start": v(471.2, 1662.43) * mm, "end": v(686.72, 1877.96) * mm});
            skLineSegment(sketch, "E116.0.6.7", {"start": v(475.68, 2097.97) * mm, "end": v(691.2, 1882.45) * mm});
            skLineSegment(sketch, "E116.3.6.7", {"start": v(906.73, 2097.97) * mm, "end": v(691.2, 2313.5) * mm});
            skLineSegment(sketch, "E116.6.6.7", {"start": v(691.2, 2313.5) * mm, "end": v(475.68, 2097.97) * mm});
            skLineSegment(sketch, "E116.9.6.7", {"start": v(691.2, 1882.45) * mm, "end": v(906.73, 2097.97) * mm});
            skLineSegment(sketch, "E117.0.7.0", {"start": v(2235.81, 777.88) * mm, "end": v(2451.34, 562.35) * mm});
            skLineSegment(sketch, "E117.3.7.0", {"start": v(2666.87, 777.88) * mm, "end": v(2451.34, 993.4) * mm});
            skLineSegment(sketch, "E117.6.7.0", {"start": v(2451.34, 993.4) * mm, "end": v(2235.81, 777.87) * mm});
            skLineSegment(sketch, "E117.9.7.0", {"start": v(2451.34, 562.35) * mm, "end": v(2666.87, 777.88) * mm});
            skLineSegment(sketch, "E117.0.7.1", {"start": v(2015.8, 997.9) * mm, "end": v(2231.32, 782.37) * mm});
            skLineSegment(sketch, "E117.3.7.1", {"start": v(2446.85, 997.9) * mm, "end": v(2231.32, 1213.42) * mm});
            skLineSegment(sketch, "E117.6.7.1", {"start": v(2231.32, 1213.42) * mm, "end": v(2015.8, 997.9) * mm});
            skLineSegment(sketch, "E117.9.7.1", {"start": v(2231.32, 782.37) * mm, "end": v(2446.85, 997.9) * mm});
            skLineSegment(sketch, "E117.0.7.2", {"start": v(1795.78, 1217.9) * mm, "end": v(2011.3, 1002.38) * mm});
            skLineSegment(sketch, "E117.3.7.2", {"start": v(2226.83, 1217.9) * mm, "end": v(2011.3, 1433.43) * mm});
            skLineSegment(sketch, "E117.6.7.2", {"start": v(2011.3, 1433.43) * mm, "end": v(1795.78, 1217.9) * mm});
            skLineSegment(sketch, "E117.9.7.2", {"start": v(2011.3, 1002.38) * mm, "end": v(2226.83, 1217.9) * mm});
            skLineSegment(sketch, "E117.0.7.3", {"start": v(1575.76, 1437.92) * mm, "end": v(1791.3, 1222.4) * mm});
            skLineSegment(sketch, "E117.3.7.3", {"start": v(2006.82, 1437.92) * mm, "end": v(1791.3, 1653.45) * mm});
            skLineSegment(sketch, "E117.6.7.3", {"start": v(1791.3, 1653.45) * mm, "end": v(1575.76, 1437.92) * mm});
            skLineSegment(sketch, "E117.9.7.3", {"start": v(1791.3, 1222.4) * mm, "end": v(2006.82, 1437.92) * mm});
            skLineSegment(sketch, "E117.0.7.4", {"start": v(1355.75, 1657.94) * mm, "end": v(1571.27, 1442.41) * mm});
            skLineSegment(sketch, "E117.3.7.4", {"start": v(1786.8, 1657.94) * mm, "end": v(1571.27, 1873.47) * mm});
            skLineSegment(sketch, "E117.6.7.4", {"start": v(1571.27, 1873.47) * mm, "end": v(1355.75, 1657.94) * mm});
            skLineSegment(sketch, "E117.9.7.4", {"start": v(1571.27, 1442.41) * mm, "end": v(1786.8, 1657.94) * mm});
            skLineSegment(sketch, "E117.0.7.5", {"start": v(1135.73, 1877.96) * mm, "end": v(1351.26, 1662.43) * mm});
            skLineSegment(sketch, "E117.3.7.5", {"start": v(1566.78, 1877.96) * mm, "end": v(1351.26, 2093.48) * mm});
            skLineSegment(sketch, "E117.6.7.5", {"start": v(1351.26, 2093.48) * mm, "end": v(1135.73, 1877.96) * mm});
            skLineSegment(sketch, "E117.9.7.5", {"start": v(1351.26, 1662.43) * mm, "end": v(1566.78, 1877.96) * mm});
            skLineSegment(sketch, "E117.0.7.6", {"start": v(915.72, 2097.97) * mm, "end": v(1131.24, 1882.45) * mm});
            skLineSegment(sketch, "E117.3.7.6", {"start": v(1346.77, 2097.97) * mm, "end": v(1131.24, 2313.5) * mm});
            skLineSegment(sketch, "E117.6.7.6", {"start": v(1131.24, 2313.5) * mm, "end": v(915.72, 2097.97) * mm});
            skLineSegment(sketch, "E117.9.7.6", {"start": v(1131.24, 1882.45) * mm, "end": v(1346.77, 2097.97) * mm});
            skLineSegment(sketch, "E117.0.7.7", {"start": v(695.7, 2317.99) * mm, "end": v(911.22, 2102.46) * mm});
            skLineSegment(sketch, "E117.3.7.7", {"start": v(1126.75, 2317.99) * mm, "end": v(911.22, 2533.52) * mm});
            skLineSegment(sketch, "E117.6.7.7", {"start": v(911.22, 2533.52) * mm, "end": v(695.7, 2317.99) * mm});
            skLineSegment(sketch, "E117.9.7.7", {"start": v(911.22, 2102.46) * mm, "end": v(1126.75, 2317.99) * mm});
            skLineSegment(sketch, "E118", {"start": v(1822.45, 777.87) * mm, "end": v(911.22, 777.87) * mm, "construction": true});
            skLineSegment(sketch, "E119", {"start": v(911.22, 1555.75) * mm, "end": v(911.22, 777.87) * mm, "construction": true});
            skLineSegment(sketch, "E120", {"start": v(1822.45, 1555.75) * mm, "end": v(0, 1555.75) * mm, "construction": true});
            skCircle(sketch, "E121", {"center": v(911.22, 777.87) * mm, "radius": 4.5 * mm, "construction": true});
            skSolve(sketch);
        }
        {
            var Q0;
            Q0=qSketchRegion(id+"F3",true);
            extrude(context, id + "F4", {"entities" : qUnion([Q0]), "oppositeDirection" : true, "depth" : 12.7 * mm, "offsetDistance" : 25.4 * mm});
        }
        {
            var Q0;
            Q0=qCreatedBy(makeId("Top.planeOp"),FACE);
            var sketch = newSketch(context, id + "F5", { "sketchPlane" : qUnion([Q0])});
            skLineSegment(sketch, "E122.1", {"start": v(0, 0) * mm, "end": v(0, 1555.75) * mm});
            skLineSegment(sketch, "E122.3", {"start": v(0, 1555.75) * mm, "end": v(1822.45, 1555.75) * mm});
            skLineSegment(sketch, "E122.4", {"start": v(1822.45, 1555.75) * mm, "end": v(1822.45, 0) * mm});
            skLineSegment(sketch, "E123", {"start": v(0, 0) * mm, "end": v(1822.45, 0) * mm});
            skLineSegment(sketch, "E124.bottom", {"start": v(-1312.2, 3120.02) * mm, "end": v(3170.7, 3120.02) * mm});
            skLineSegment(sketch, "E124.top", {"start": v(-1312.2, -1365.39) * mm, "end": v(3170.7, -1365.39) * mm});
            skLineSegment(sketch, "E124.left", {"start": v(-1312.2, 3120.02) * mm, "end": v(-1312.2, -1365.39) * mm});
            skLineSegment(sketch, "E124.right", {"start": v(3170.7, 3120.02) * mm, "end": v(3170.7, -1365.39) * mm});
            skSolve(sketch);
        }
        {
            var Q0;
            Q0=qSketchRegion(id+"F5",true);
            extrude(context, id + "F6", {"entities" : qUnion([Q0]), "operationType" : NewBodyOperationType.REMOVE, "oppositeDirection" : true, "depth" : 76.2 * mm, "offsetDistance" : 25.4 * mm});
        }
        {
            var Q0;
            Q0=qCreatedBy(makeId("Top.planeOp"),FACE);
            var sketch = newSketch(context, id + "F7", { "sketchPlane" : qUnion([Q0])});
            skLineSegment(sketch, "E125.bottom", {"start": v(0, 1555.75) * mm, "end": v(1454.15, 1555.75) * mm});
            skLineSegment(sketch, "E125.top", {"start": v(0, 2298.7) * mm, "end": v(1454.15, 2298.7) * mm});
            skLineSegment(sketch, "E125.left", {"start": v(0, 1555.75) * mm, "end": v(0, 2298.7) * mm});
            skLineSegment(sketch, "E125.right", {"start": v(1454.15, 1555.75) * mm, "end": v(1454.15, 2298.7) * mm});
            skSolve(sketch);
        }
        {
            var Q0;
            Q0=qSketchRegion(id+"F7",true);
            extrude(context, id + "F8", {"entities" : qUnion([Q0]), "depth" : 431.8 * mm, "offsetDistance" : 25.4 * mm});
        }
        {
            var Q0;
            Q0=makeQuery(id+"F8.opExtrude","CAP_FACE",FACE,{"disambiguationData":[OSD([sQuery(id+"F7.wireOp",EDGE,"E125.bottom"),sQuery(id+"F7.wireOp",EDGE,"E125.top"),sQuery(id+"F7.wireOp",EDGE,"E125.left"),sQuery(id+"F7.wireOp",EDGE,"E125.right")])],"isStart":false});
            var sketch = newSketch(context, id + "F9", { "sketchPlane" : qUnion([Q0])});
            skLineSegment(sketch, "E126.0", {"start": v(1352.55, 2197.1) * mm, "end": v(101.6, 2197.1) * mm});
            skLineSegment(sketch, "E126.1", {"start": v(1352.55, 1657.35) * mm, "end": v(1352.55, 2197.1) * mm});
            skLineSegment(sketch, "E126.2", {"start": v(101.6, 1657.35) * mm, "end": v(1352.55, 1657.35) * mm});
            skLineSegment(sketch, "E126.3", {"start": v(101.6, 2197.1) * mm, "end": v(101.6, 1657.35) * mm});
            skSolve(sketch);
        }
        {
            var Q0;
            Q0=qSketchRegion(id+"F9",true);
            extrude(context, id + "F10", {"entities" : qUnion([Q0]), "operationType" : NewBodyOperationType.REMOVE, "oppositeDirection" : true, "depth" : 381 * mm, "offsetDistance" : 25.4 * mm});
        }
        {
            var Q0;
            Q0=makeQuery(id+"F10.boolean.opBoolean","COPY",EDGE,{"derivedFrom":makeQuery(id+"F10.opExtrude","SWEPT_EDGE",EDGE,{"disambiguationData":[OSD([sQuery(id+"F9.wireOp",EDGE,"E126.0"),sQuery(id+"F9.wireOp",EDGE,"E126.3")])]})});
            var Q1;
            Q1=makeQuery(id+"F10.boolean.opBoolean","COPY",EDGE,{"derivedFrom":makeQuery(id+"F10.opExtrude","SWEPT_EDGE",EDGE,{"disambiguationData":[OSD([sQuery(id+"F9.wireOp",EDGE,"E126.2"),sQuery(id+"F9.wireOp",EDGE,"E126.3")])]})});
            var Q2;
            Q2=makeQuery(id+"F10.boolean.opBoolean","COPY",EDGE,{"derivedFrom":makeQuery(id+"F10.opExtrude","SWEPT_EDGE",EDGE,{"disambiguationData":[OSD([sQuery(id+"F9.wireOp",EDGE,"E126.0"),sQuery(id+"F9.wireOp",EDGE,"E126.1")])]})});
            var Q3;
            Q3=makeQuery(id+"F10.boolean.opBoolean","COPY",EDGE,{"derivedFrom":makeQuery(id+"F10.opExtrude","SWEPT_EDGE",EDGE,{"disambiguationData":[OSD([sQuery(id+"F9.wireOp",EDGE,"E126.1"),sQuery(id+"F9.wireOp",EDGE,"E126.2")])]})});
            fillet(context, id + "F11", {"entities" : qUnion([Q0, Q1, Q2, Q3]), "radius" : 50.8 * mm, "tangentPropagation" : true, "allowEdgeOverflow" : false});
        }
        {
            var Q0;
            Q0=makeQuery(id+"F10.boolean.opBoolean","COPY",EDGE,{"derivedFrom":makeQuery(id+"F10.opExtrude","CAP_EDGE",EDGE,{"disambiguationData":[OSD([sQuery(id+"F9.wireOp",EDGE,"E126.1")])],"isStart":false})});
            fillet(context, id + "F12", {"entities" : qUnion([Q0]), "radius" : 101.6 * mm, "tangentPropagation" : true, "allowEdgeOverflow" : false});
        }
        {
            var Q0;
            Q0=makeQuery(id+"F8.opExtrude","CAP_EDGE",EDGE,{"disambiguationData":[OSD([sQuery(id+"F7.wireOp",EDGE,"E125.bottom")])],"isStart":false});
            var Q1;
            Q1=makeQuery(id+"F10.boolean.opBoolean","COPY",EDGE,{"derivedFrom":makeQuery(id+"F10.opExtrude","CAP_EDGE",EDGE,{"disambiguationData":[OSD([sQuery(id+"F9.wireOp",EDGE,"E126.0")])],"isStart":true})});
            fillet(context, id + "F13", {"entities" : qUnion([Q0, Q1]), "radius" : 50.8 * mm, "tangentPropagation" : true, "allowEdgeOverflow" : false});
        }
        {
            var Q0;
            Q0=qCreatedBy(makeId("Top.planeOp"),FACE);
            var sketch = newSketch(context, id + "F14", { "sketchPlane" : qUnion([Q0])});
            skLineSegment(sketch, "E127.bottom", {"start": v(298.45, 1420.28) * mm, "end": v(0, 1420.28) * mm});
            skLineSegment(sketch, "E127.top", {"start": v(298.45, 1401.23) * mm, "end": v(0, 1401.23) * mm});
            skLineSegment(sketch, "E127.left", {"start": v(298.45, 1420.28) * mm, "end": v(298.45, 1401.23) * mm});
            skLineSegment(sketch, "E127.right", {"start": v(0, 1420.28) * mm, "end": v(0, 1401.23) * mm});
            skLineSegment(sketch, "E128.bottom", {"start": v(298.45, 745.07) * mm, "end": v(38.1, 745.07) * mm});
            skLineSegment(sketch, "E128.top", {"start": v(298.45, 726.02) * mm, "end": v(38.1, 726.02) * mm});
            skLineSegment(sketch, "E128.left", {"start": v(298.45, 745.07) * mm, "end": v(298.45, 726.02) * mm});
            skLineSegment(sketch, "E128.right", {"start": v(38.1, 745.07) * mm, "end": v(38.1, 726.02) * mm});
            skLineSegment(sketch, "E129.bottom", {"start": v(38.1, 713.32) * mm, "end": v(501.65, 713.32) * mm});
            skLineSegment(sketch, "E129.top", {"start": v(38.1, 694.27) * mm, "end": v(501.65, 694.27) * mm});
            skLineSegment(sketch, "E129.left", {"start": v(38.1, 713.32) * mm, "end": v(38.1, 694.27) * mm});
            skLineSegment(sketch, "E129.right", {"start": v(501.65, 713.32) * mm, "end": v(501.65, 694.27) * mm});
            skLineSegment(sketch, "E130.bottom", {"start": v(501.65, 25.4) * mm, "end": v(0, 25.4) * mm});
            skLineSegment(sketch, "E130.top", {"start": v(501.65, 6.35) * mm, "end": v(0, 6.35) * mm});
            skLineSegment(sketch, "E130.left", {"start": v(501.65, 25.4) * mm, "end": v(501.65, 6.35) * mm});
            skLineSegment(sketch, "E130.right", {"start": v(0, 25.4) * mm, "end": v(0, 6.35) * mm});
            skSolve(sketch);
        }
        {
            var Q0;
            Q0=qSketchRegion(id+"F14",true);
            extrude(context, id + "F15", {"entities" : qUnion([Q0]), "depth" : 889 * mm, "offsetDistance" : 25.4 * mm});
        }
        {
            var Q0;
            Q0=qCreatedBy(makeId("Top.planeOp"),FACE);
            var sketch = newSketch(context, id + "F16", { "sketchPlane" : qUnion([Q0])});
            skLineSegment(sketch, "E131.bottom", {"start": v(38.1, 726.02) * mm, "end": v(298.45, 726.02) * mm});
            skLineSegment(sketch, "E131.top", {"start": v(38.1, 713.32) * mm, "end": v(298.45, 713.32) * mm});
            skLineSegment(sketch, "E131.left", {"start": v(38.1, 726.02) * mm, "end": v(38.1, 713.32) * mm});
            skLineSegment(sketch, "E131.right", {"start": v(298.45, 726.02) * mm, "end": v(298.45, 713.32) * mm});
            skSolve(sketch);
        }
        {
            var Q0;
            Q0=qSketchRegion(id+"F16",true);
            var Q1;
            Q1=makeQuery(id+"F15.opExtrude","CAP_FACE",FACE,{"disambiguationData":[OSD([sQuery(id+"F14.wireOp",EDGE,"E129.bottom"),sQuery(id+"F14.wireOp",EDGE,"E129.top"),sQuery(id+"F14.wireOp",EDGE,"E129.left"),sQuery(id+"F14.wireOp",EDGE,"E129.right")])],"isStart":false});
            extrude(context, id + "F17", {"entities" : qUnion([Q0]), "endBound" : BoundingType.UP_TO_SURFACE, "depth" : 25.4 * mm, "endBoundEntityFace" : qUnion([Q1]), "offsetDistance" : 25.4 * mm});
        }
        {
            var Q0;
            Q0=makeQuery(id+"F15.opExtrude","SWEPT_FACE",FACE,{"disambiguationData":[OSD([sQuery(id+"F14.wireOp",EDGE,"E130.top")])]});
            var sketch = newSketch(context, id + "F18", { "sketchPlane" : qUnion([Q0])});
            skLineSegment(sketch, "E132.bottom", {"start": v(501.65, 0) * mm, "end": v(425.45, 0) * mm});
            skLineSegment(sketch, "E132.top", {"start": v(501.65, 101.6) * mm, "end": v(425.45, 101.6) * mm});
            skLineSegment(sketch, "E132.left", {"start": v(501.65, 0) * mm, "end": v(501.65, 101.6) * mm});
            skLineSegment(sketch, "E132.right", {"start": v(425.45, 0) * mm, "end": v(425.45, 101.6) * mm});
            skSolve(sketch);
        }
        {
            var Q0;
            Q0=qSketchRegion(id+"F18",true);
            var Q1;
            Q1=makeQuery(id+"F15.opExtrude","SWEPT_FACE",FACE,{"disambiguationData":[OSD([sQuery(id+"F14.wireOp",EDGE,"E129.bottom")])]});
            extrude(context, id + "F19", {"entities" : qUnion([Q0]), "operationType" : NewBodyOperationType.REMOVE, "endBound" : BoundingType.UP_TO_SURFACE, "oppositeDirection" : true, "depth" : 25.4 * mm, "endBoundEntityFace" : qUnion([Q1]), "offsetDistance" : 25.4 * mm});
        }
        {
            var Q0;
            Q0=makeQuery(id+"F15.opExtrude","SWEPT_FACE",FACE,{"disambiguationData":[OSD([sQuery(id+"F14.wireOp",EDGE,"E130.bottom")])]});
            var sketch = newSketch(context, id + "F20", { "sketchPlane" : qUnion([Q0])});
            skLineSegment(sketch, "E133.bottom", {"start": v(-501.65, 114.3) * mm, "end": v(-19.05, 114.3) * mm});
            skLineSegment(sketch, "E133.top", {"start": v(-501.65, 133.35) * mm, "end": v(-19.05, 133.35) * mm});
            skLineSegment(sketch, "E133.left", {"start": v(-501.65, 114.3) * mm, "end": v(-501.65, 133.35) * mm});
            skLineSegment(sketch, "E133.right", {"start": v(-19.05, 114.3) * mm, "end": v(-19.05, 133.35) * mm});
            skSolve(sketch);
        }
        {
            var Q0;
            Q0=qSketchRegion(id+"F20",true);
            var Q1;
            Q1=makeQuery(id+"F15.opExtrude","SWEPT_FACE",FACE,{"disambiguationData":[OSD([sQuery(id+"F14.wireOp",EDGE,"E129.top")])]});
            extrude(context, id + "F21", {"entities" : qUnion([Q0]), "endBound" : BoundingType.UP_TO_SURFACE, "depth" : 25.4 * mm, "endBoundEntityFace" : qUnion([Q1]), "offsetDistance" : 25.4 * mm});
        }
        {
            var Q0;
            Q0=makeQuery(id+"F15.opExtrude","SWEPT_FACE",FACE,{"disambiguationData":[OSD([sQuery(id+"F14.wireOp",EDGE,"E130.left")])]});
            var sketch = newSketch(context, id + "F22", { "sketchPlane" : qUnion([Q0])});
            skLineSegment(sketch, "E134.bottom", {"start": v(38.1, 98.43) * mm, "end": v(0, 98.43) * mm});
            skLineSegment(sketch, "E134.top", {"start": v(38.1, 889) * mm, "end": v(0, 889) * mm});
            skLineSegment(sketch, "E134.left", {"start": v(38.1, 98.43) * mm, "end": v(38.1, 889) * mm});
            skLineSegment(sketch, "E134.right", {"start": v(0, 98.43) * mm, "end": v(0, 889) * mm});
            skLineSegment(sketch, "E135.bottom", {"start": v(719.67, 98.43) * mm, "end": v(681.57, 98.43) * mm});
            skLineSegment(sketch, "E135.top", {"start": v(719.67, 889) * mm, "end": v(681.57, 889) * mm});
            skLineSegment(sketch, "E135.left", {"start": v(719.67, 98.43) * mm, "end": v(719.67, 889) * mm});
            skLineSegment(sketch, "E135.right", {"start": v(681.57, 98.43) * mm, "end": v(681.57, 889) * mm});
            skLineSegment(sketch, "E136", {"start": v(38.1, 98.43) * mm, "end": v(681.57, 98.43) * mm, "construction": true});
            skLineSegment(sketch, "E137", {"start": v(681.57, 136.53) * mm, "end": v(38.1, 136.53) * mm, "construction": true});
            skSolve(sketch);
        }
        {
            var Q0;
            Q0=qSketchRegion(id+"F22",true);
            extrude(context, id + "F23", {"entities" : qUnion([Q0]), "depth" : 19.05 * mm, "offsetDistance" : 25.4 * mm});
        }
        {
            var Q0;
            Q0=makeQuery(id+"F23.opExtrude","SWEPT_FACE",FACE,{"disambiguationData":[OSD([sQuery(id+"F22.wireOp",EDGE,"E134.left")])]});
            var sketch = newSketch(context, id + "F24", { "sketchPlane" : qUnion([Q0])});
            skLineSegment(sketch, "E138.bottom", {"start": v(-520.7, 98.43) * mm, "end": v(-501.65, 98.43) * mm});
            skLineSegment(sketch, "E138.top", {"start": v(-520.7, 136.53) * mm, "end": v(-501.65, 136.53) * mm});
            skLineSegment(sketch, "E138.left", {"start": v(-520.7, 98.43) * mm, "end": v(-520.7, 136.53) * mm});
            skLineSegment(sketch, "E138.right", {"start": v(-501.65, 98.43) * mm, "end": v(-501.65, 136.53) * mm});
            skLineSegment(sketch, "E139.bottom", {"start": v(-520.7, 889) * mm, "end": v(-501.65, 889) * mm});
            skLineSegment(sketch, "E139.top", {"start": v(-520.7, 850.9) * mm, "end": v(-501.65, 850.9) * mm});
            skLineSegment(sketch, "E139.left", {"start": v(-520.7, 889) * mm, "end": v(-520.7, 850.9) * mm});
            skLineSegment(sketch, "E139.right", {"start": v(-501.65, 889) * mm, "end": v(-501.65, 850.9) * mm});
            skSolve(sketch);
        }
        {
            var Q0;
            Q0=qSketchRegion(id+"F24",true);
            var Q1;
            Q1=makeQuery(id+"F23.opExtrude","SWEPT_BODY",BODY,{"disambiguationData":[OSD([sQuery(id+"F22.wireOp",EDGE,"E135.bottom"),sQuery(id+"F22.wireOp",EDGE,"E135.top"),sQuery(id+"F22.wireOp",EDGE,"E135.left"),sQuery(id+"F22.wireOp",EDGE,"E135.right")])]});
            extrude(context, id + "F25", {"entities" : qUnion([Q0]), "endBound" : BoundingType.UP_TO_BODY, "depth" : 25.4 * mm, "endBoundEntityBody" : qUnion([Q1]), "offsetDistance" : 25.4 * mm});
        }
        {
            var Q0;
            Q0=makeQuery(id+"F15.opExtrude","SWEPT_FACE",FACE,{"disambiguationData":[OSD([sQuery(id+"F14.wireOp",EDGE,"E128.left")])]});
            var sketch = newSketch(context, id + "F26", { "sketchPlane" : qUnion([Q0])});
            skLineSegment(sketch, "E140.bottom", {"start": v(1432.98, 0) * mm, "end": v(1394.88, 0) * mm});
            skLineSegment(sketch, "E140.top", {"start": v(1432.98, 889) * mm, "end": v(1394.88, 889) * mm});
            skLineSegment(sketch, "E140.left", {"start": v(1432.98, 0) * mm, "end": v(1432.98, 889) * mm});
            skLineSegment(sketch, "E140.right", {"start": v(1394.88, 0) * mm, "end": v(1394.88, 889) * mm});
            skLineSegment(sketch, "E141.bottom", {"start": v(713.32, 889) * mm, "end": v(751.42, 889) * mm});
            skLineSegment(sketch, "E141.top", {"start": v(713.32, 0) * mm, "end": v(751.42, 0) * mm});
            skLineSegment(sketch, "E141.left", {"start": v(713.32, 889) * mm, "end": v(713.32, 0) * mm});
            skLineSegment(sketch, "E141.right", {"start": v(751.42, 889) * mm, "end": v(751.42, 0) * mm});
            skSolve(sketch);
        }
        {
            var Q0;
            Q0=qSketchRegion(id+"F26",true);
            extrude(context, id + "F27", {"entities" : qUnion([Q0]), "depth" : 19.05 * mm, "offsetDistance" : 25.4 * mm});
        }
        {
            var Q0;
            Q0=makeQuery(id+"F27.opExtrude","SWEPT_FACE",FACE,{"disambiguationData":[OSD([sQuery(id+"F26.wireOp",EDGE,"E141.right")])]});
            var sketch = newSketch(context, id + "F28", { "sketchPlane" : qUnion([Q0])});
            skLineSegment(sketch, "E142.bottom", {"start": v(-317.5, 889) * mm, "end": v(-298.45, 889) * mm});
            skLineSegment(sketch, "E142.top", {"start": v(-317.5, 850.9) * mm, "end": v(-298.45, 850.9) * mm});
            skLineSegment(sketch, "E142.left", {"start": v(-317.5, 889) * mm, "end": v(-317.5, 850.9) * mm});
            skLineSegment(sketch, "E142.right", {"start": v(-298.45, 889) * mm, "end": v(-298.45, 850.9) * mm});
            skLineSegment(sketch, "E143.bottom", {"start": v(-298.45, 0) * mm, "end": v(-317.5, 0) * mm});
            skLineSegment(sketch, "E143.top", {"start": v(-298.45, 127) * mm, "end": v(-317.5, 127) * mm});
            skLineSegment(sketch, "E143.left", {"start": v(-298.45, 0) * mm, "end": v(-298.45, 127) * mm});
            skLineSegment(sketch, "E143.right", {"start": v(-317.5, 0) * mm, "end": v(-317.5, 127) * mm});
            skLineSegment(sketch, "E144.bottom", {"start": v(-317.5, 698.5) * mm, "end": v(-298.45, 698.5) * mm});
            skLineSegment(sketch, "E144.top", {"start": v(-317.5, 660.4) * mm, "end": v(-298.45, 660.4) * mm});
            skLineSegment(sketch, "E144.left", {"start": v(-317.5, 698.5) * mm, "end": v(-317.5, 660.4) * mm});
            skLineSegment(sketch, "E144.right", {"start": v(-298.45, 698.5) * mm, "end": v(-298.45, 660.4) * mm});
            skLineSegment(sketch, "E145.bottom", {"start": v(-317.5, 508) * mm, "end": v(-298.45, 508) * mm});
            skLineSegment(sketch, "E145.top", {"start": v(-317.5, 469.9) * mm, "end": v(-298.45, 469.9) * mm});
            skLineSegment(sketch, "E145.left", {"start": v(-317.5, 508) * mm, "end": v(-317.5, 469.9) * mm});
            skLineSegment(sketch, "E145.right", {"start": v(-298.45, 508) * mm, "end": v(-298.45, 469.9) * mm});
            skLineSegment(sketch, "E146", {"start": v(-317.5, 660.4) * mm, "end": v(-317.5, 508) * mm, "construction": true});
            skLineSegment(sketch, "E147", {"start": v(-317.5, 698.5) * mm, "end": v(-317.5, 850.9) * mm, "construction": true});
            skLineSegment(sketch, "E148.bottom", {"start": v(-317.5, 317.5) * mm, "end": v(-298.45, 317.5) * mm});
            skLineSegment(sketch, "E148.top", {"start": v(-317.5, 279.4) * mm, "end": v(-298.45, 279.4) * mm});
            skLineSegment(sketch, "E148.left", {"start": v(-317.5, 317.5) * mm, "end": v(-317.5, 279.4) * mm});
            skLineSegment(sketch, "E148.right", {"start": v(-298.45, 317.5) * mm, "end": v(-298.45, 279.4) * mm});
            skLineSegment(sketch, "E149", {"start": v(-317.5, 469.9) * mm, "end": v(-317.5, 317.5) * mm, "construction": true});
            skLineSegment(sketch, "E150", {"start": v(-317.5, 279.4) * mm, "end": v(-317.5, 127) * mm, "construction": true});
            skSolve(sketch);
        }
        {
            var Q0;
            Q0=qSketchRegion(id+"F28",true);
            var Q1;
            Q1=makeQuery(id+"F27.opExtrude","SWEPT_BODY",BODY,{"disambiguationData":[OSD([sQuery(id+"F26.wireOp",EDGE,"E140.bottom"),sQuery(id+"F26.wireOp",EDGE,"E140.top"),sQuery(id+"F26.wireOp",EDGE,"E140.left"),sQuery(id+"F26.wireOp",EDGE,"E140.right")])]});
            extrude(context, id + "F29", {"entities" : qUnion([Q0]), "endBound" : BoundingType.UP_TO_BODY, "depth" : 25.4 * mm, "endBoundEntityBody" : qUnion([Q1]), "offsetDistance" : 25.4 * mm});
        }
        {
            var Q0;
            Q0=makeQuery(id+"F27.opExtrude","CAP_FACE",FACE,{"disambiguationData":[OSD([sQuery(id+"F26.wireOp",EDGE,"E141.bottom"),sQuery(id+"F26.wireOp",EDGE,"E141.top"),sQuery(id+"F26.wireOp",EDGE,"E141.left"),sQuery(id+"F26.wireOp",EDGE,"E141.right")])],"isStart":false});
            var sketch = newSketch(context, id + "F30", { "sketchPlane" : qUnion([Q0])});
            skLineSegment(sketch, "E151.bottom", {"start": v(732.37, 485.77) * mm, "end": v(1413.93, 485.78) * mm});
            skLineSegment(sketch, "E151.top", {"start": v(732.37, 301.62) * mm, "end": v(1413.93, 301.63) * mm});
            skLineSegment(sketch, "E151.left", {"start": v(732.37, 485.77) * mm, "end": v(732.37, 301.62) * mm});
            skLineSegment(sketch, "E151.right", {"start": v(1413.93, 485.78) * mm, "end": v(1413.93, 301.63) * mm});
            skLineSegment(sketch, "E152.bottom", {"start": v(1413.93, 492.13) * mm, "end": v(732.37, 492.12) * mm});
            skLineSegment(sketch, "E152.top", {"start": v(1413.93, 676.28) * mm, "end": v(732.37, 676.28) * mm});
            skLineSegment(sketch, "E152.left", {"start": v(1413.93, 492.13) * mm, "end": v(1413.93, 676.28) * mm});
            skLineSegment(sketch, "E152.right", {"start": v(732.37, 492.12) * mm, "end": v(732.37, 676.28) * mm});
            skLineSegment(sketch, "E153.bottom", {"start": v(732.37, 866.77) * mm, "end": v(1413.93, 866.78) * mm});
            skLineSegment(sketch, "E153.top", {"start": v(732.37, 682.62) * mm, "end": v(1413.93, 682.63) * mm});
            skLineSegment(sketch, "E153.left", {"start": v(732.37, 866.78) * mm, "end": v(732.37, 682.62) * mm});
            skLineSegment(sketch, "E153.right", {"start": v(1413.93, 866.78) * mm, "end": v(1413.93, 682.63) * mm});
            skLineSegment(sketch, "E154.bottom", {"start": v(732.37, 295.27) * mm, "end": v(1413.93, 295.28) * mm});
            skLineSegment(sketch, "E154.top", {"start": v(732.37, 111.12) * mm, "end": v(1413.93, 111.13) * mm});
            skLineSegment(sketch, "E154.left", {"start": v(732.37, 295.27) * mm, "end": v(732.37, 111.12) * mm});
            skLineSegment(sketch, "E154.right", {"start": v(1413.93, 295.28) * mm, "end": v(1413.93, 111.13) * mm});
            skSolve(sketch);
        }
        {
            var Q0;
            Q0=qSketchRegion(id+"F30",true);
            extrude(context, id + "F31", {"entities" : qUnion([Q0]), "depth" : 19.05 * mm, "offsetDistance" : 25.4 * mm});
        }
        {
            var Q0;
            Q0=makeQuery(id+"F31.opExtrude","CAP_FACE",FACE,{"disambiguationData":[OSD([sQuery(id+"F30.wireOp",EDGE,"E153.bottom"),sQuery(id+"F30.wireOp",EDGE,"E153.top"),sQuery(id+"F30.wireOp",EDGE,"E153.left"),sQuery(id+"F30.wireOp",EDGE,"E153.right")])],"isStart":false});
            var sketch = newSketch(context, id + "F32", { "sketchPlane" : qUnion([Q0])});
            skLineSegment(sketch, "E155.0", {"start": v(1363.13, 815.98) * mm, "end": v(783.17, 815.98) * mm});
            skLineSegment(sketch, "E155.1", {"start": v(1363.13, 733.43) * mm, "end": v(1363.13, 815.98) * mm});
            skLineSegment(sketch, "E155.2", {"start": v(783.17, 733.43) * mm, "end": v(1363.13, 733.43) * mm});
            skLineSegment(sketch, "E155.3", {"start": v(783.17, 815.98) * mm, "end": v(783.17, 733.43) * mm});
            skLineSegment(sketch, "E156.0", {"start": v(1363.13, 542.93) * mm, "end": v(1363.13, 625.48) * mm});
            skLineSegment(sketch, "E156.1", {"start": v(783.17, 542.92) * mm, "end": v(1363.13, 542.93) * mm});
            skLineSegment(sketch, "E156.2", {"start": v(783.17, 625.48) * mm, "end": v(783.17, 542.92) * mm});
            skLineSegment(sketch, "E156.3", {"start": v(1363.13, 625.48) * mm, "end": v(783.17, 625.48) * mm});
            skLineSegment(sketch, "E157.0", {"start": v(783.17, 434.98) * mm, "end": v(783.17, 352.43) * mm});
            skLineSegment(sketch, "E157.1", {"start": v(1363.13, 434.98) * mm, "end": v(783.17, 434.98) * mm});
            skLineSegment(sketch, "E157.2", {"start": v(1363.13, 352.43) * mm, "end": v(1363.13, 434.98) * mm});
            skLineSegment(sketch, "E157.3", {"start": v(783.17, 352.43) * mm, "end": v(1363.13, 352.43) * mm});
            skLineSegment(sketch, "E158.0", {"start": v(1363.13, 244.48) * mm, "end": v(783.17, 244.47) * mm});
            skLineSegment(sketch, "E158.1", {"start": v(1363.13, 161.93) * mm, "end": v(1363.13, 244.48) * mm});
            skLineSegment(sketch, "E158.2", {"start": v(783.17, 161.92) * mm, "end": v(1363.13, 161.93) * mm});
            skLineSegment(sketch, "E158.3", {"start": v(783.17, 244.47) * mm, "end": v(783.17, 161.92) * mm});
            skSolve(sketch);
        }
        {
            var Q0;
            Q0=qSketchRegion(id+"F32",true);
            extrude(context, id + "F33", {"entities" : qUnion([Q0]), "operationType" : NewBodyOperationType.REMOVE, "oppositeDirection" : true, "depth" : 6.35 * mm, "offsetDistance" : 25.4 * mm});
        }
        {
            var Q0;
            Q0=makeQuery(id+"F23.opExtrude","CAP_FACE",FACE,{"disambiguationData":[OSD([sQuery(id+"F22.wireOp",EDGE,"E135.bottom"),sQuery(id+"F22.wireOp",EDGE,"E135.top"),sQuery(id+"F22.wireOp",EDGE,"E135.left"),sQuery(id+"F22.wireOp",EDGE,"E135.right")])],"isStart":false});
            var sketch = newSketch(context, id + "F34", { "sketchPlane" : qUnion([Q0])});
            skLineSegment(sketch, "E159.bottom", {"start": v(706.97, 866.78) * mm, "end": v(361.42, 866.78) * mm});
            skLineSegment(sketch, "E159.top", {"start": v(706.97, 111.13) * mm, "end": v(361.42, 111.13) * mm});
            skLineSegment(sketch, "E159.left", {"start": v(706.97, 866.78) * mm, "end": v(706.97, 111.13) * mm});
            skLineSegment(sketch, "E159.right", {"start": v(361.42, 866.78) * mm, "end": v(361.42, 111.13) * mm});
            skLineSegment(sketch, "E160.bottom", {"start": v(358.25, 111.13) * mm, "end": v(12.7, 111.13) * mm});
            skLineSegment(sketch, "E160.top", {"start": v(358.25, 866.78) * mm, "end": v(12.7, 866.78) * mm});
            skLineSegment(sketch, "E160.left", {"start": v(358.25, 111.13) * mm, "end": v(358.25, 866.78) * mm});
            skLineSegment(sketch, "E160.right", {"start": v(12.7, 111.13) * mm, "end": v(12.7, 866.77) * mm});
            skSolve(sketch);
        }
        {
            var Q0;
            Q0=qSketchRegion(id+"F34",true);
            extrude(context, id + "F35", {"entities" : qUnion([Q0]), "depth" : 19.05 * mm, "offsetDistance" : 25.4 * mm});
        }
        {
            var Q0;
            Q0=makeQuery(id+"F35.opExtrude","CAP_FACE",FACE,{"disambiguationData":[OSD([sQuery(id+"F34.wireOp",EDGE,"E160.bottom"),sQuery(id+"F34.wireOp",EDGE,"E160.top"),sQuery(id+"F34.wireOp",EDGE,"E160.left"),sQuery(id+"F34.wireOp",EDGE,"E160.right")])],"isStart":false});
            var sketch = newSketch(context, id + "F36", { "sketchPlane" : qUnion([Q0])});
            skLineSegment(sketch, "E161.0", {"start": v(307.45, 161.93) * mm, "end": v(307.45, 815.98) * mm});
            skLineSegment(sketch, "E161.1", {"start": v(63.5, 161.93) * mm, "end": v(307.45, 161.93) * mm});
            skLineSegment(sketch, "E161.2", {"start": v(63.5, 815.98) * mm, "end": v(63.5, 161.93) * mm});
            skLineSegment(sketch, "E161.3", {"start": v(307.45, 815.98) * mm, "end": v(63.5, 815.98) * mm});
            skLineSegment(sketch, "E162.0", {"start": v(412.22, 161.93) * mm, "end": v(656.17, 161.93) * mm});
            skLineSegment(sketch, "E162.1", {"start": v(412.22, 815.98) * mm, "end": v(412.22, 161.93) * mm});
            skLineSegment(sketch, "E162.2", {"start": v(656.17, 815.98) * mm, "end": v(412.22, 815.98) * mm});
            skLineSegment(sketch, "E162.3", {"start": v(656.17, 161.93) * mm, "end": v(656.17, 815.98) * mm});
            skSolve(sketch);
        }
        {
            var Q0;
            Q0=qSketchRegion(id+"F36",true);
            extrude(context, id + "F37", {"entities" : qUnion([Q0]), "operationType" : NewBodyOperationType.REMOVE, "oppositeDirection" : true, "depth" : 6.35 * mm, "offsetDistance" : 25.4 * mm});
        }
        {
            var Q0;
            {var subQ0=sQuery(id+"F14.wireOp",EDGE,"E130.bottom");Q0=makeQuery(id+"F19.boolean.opBoolean","COPY",FACE,{"disambiguationData":[TD([makeQuery(id+"F15.opExtrude","SWEPT_FACE",FACE,{"disambiguationData":[OSD([subQ0])]})])],"derivedFrom":makeQuery(id+"F19.opExtrude","SWEPT_FACE",FACE,{"disambiguationData":[OSD([sQuery(id+"F18.wireOp",EDGE,"E132.right")])]})});}
            var sketch = newSketch(context, id + "F38", { "sketchPlane" : qUnion([Q0])});
            skLineSegment(sketch, "E163.bottom", {"start": v(6.35, 0) * mm, "end": v(713.32, 0) * mm});
            skLineSegment(sketch, "E163.top", {"start": v(6.35, 101.6) * mm, "end": v(713.32, 101.6) * mm});
            skLineSegment(sketch, "E163.left", {"start": v(6.35, 0) * mm, "end": v(6.35, 101.6) * mm});
            skLineSegment(sketch, "E163.right", {"start": v(713.32, 0) * mm, "end": v(713.32, 101.6) * mm});
            skSolve(sketch);
        }
        {
            var Q0;
            Q0=qSketchRegion(id+"F38",true);
            extrude(context, id + "F39", {"entities" : qUnion([Q0]), "depth" : 12.7 * mm, "offsetDistance" : 25.4 * mm});
        }
        {
            var Q0;
            Q0=makeQuery(id+"F31.opExtrude","CAP_FACE",FACE,{"disambiguationData":[OSD([sQuery(id+"F30.wireOp",EDGE,"E151.bottom"),sQuery(id+"F30.wireOp",EDGE,"E151.top"),sQuery(id+"F30.wireOp",EDGE,"E151.left"),sQuery(id+"F30.wireOp",EDGE,"E151.right")])],"isStart":true});
            var sketch = newSketch(context, id + "F40", { "sketchPlane" : qUnion([Q0])});
            skLineSegment(sketch, "E164.bottom", {"start": v(-1388.53, 139.7) * mm, "end": v(-757.77, 139.7) * mm});
            skLineSegment(sketch, "E164.top", {"start": v(-1388.53, 419.1) * mm, "end": v(-757.77, 419.1) * mm});
            skLineSegment(sketch, "E164.left", {"start": v(-1388.53, 139.7) * mm, "end": v(-1388.53, 419.1) * mm});
            skLineSegment(sketch, "E164.right", {"start": v(-757.77, 139.7) * mm, "end": v(-757.77, 419.1) * mm});
            skSolve(sketch);
        }
        {
            var Q0;
            Q0=qSketchRegion(id+"F40",true);
            var Q1;
            Q1=sQuery(id+"F2.wireOp",VERTEX,"E69.end");
            extrude(context, id + "F41", {"entities" : qUnion([Q0]), "operationType" : NewBodyOperationType.ADD, "endBound" : BoundingType.UP_TO_VERTEX, "depth" : 25.4 * mm, "endBoundEntityVertex" : qUnion([Q1]), "offsetDistance" : 25.4 * mm});
        }
        {
            var Q0;
            Q0=makeQuery(id+"F41.opExtrude","SWEPT_FACE",FACE,{"disambiguationData":[OSD([sQuery(id+"F40.wireOp",EDGE,"E164.top")])]});
            var sketch = newSketch(context, id + "F42", { "sketchPlane" : qUnion([Q0])});
            skLineSegment(sketch, "E165.0", {"start": v(304.8, 1375.83) * mm, "end": v(76.2, 1375.83) * mm});
            skLineSegment(sketch, "E165.1", {"start": v(304.8, 770.47) * mm, "end": v(304.8, 1375.83) * mm});
            skLineSegment(sketch, "E165.2", {"start": v(76.2, 770.47) * mm, "end": v(304.8, 770.47) * mm});
            skLineSegment(sketch, "E165.3", {"start": v(76.2, 1375.83) * mm, "end": v(76.2, 770.47) * mm});
            skSolve(sketch);
        }
        {
            var Q0;
            Q0=qSketchRegion(id+"F42",true);
            extrude(context, id + "F43", {"entities" : qUnion([Q0]), "operationType" : NewBodyOperationType.REMOVE, "oppositeDirection" : true, "depth" : 139.7 * mm, "offsetDistance" : 25.4 * mm});
        }
        {
            var Q0;
            Q0=makeQuery(id+"F31.opExtrude","CAP_FACE",FACE,{"disambiguationData":[OSD([sQuery(id+"F30.wireOp",EDGE,"E152.bottom"),sQuery(id+"F30.wireOp",EDGE,"E152.top"),sQuery(id+"F30.wireOp",EDGE,"E152.left"),sQuery(id+"F30.wireOp",EDGE,"E152.right")])],"isStart":true});
            var sketch = newSketch(context, id + "F44", { "sketchPlane" : qUnion([Q0])});
            skLineSegment(sketch, "E166.bottom", {"start": v(-1388.53, 609.6) * mm, "end": v(-757.77, 609.6) * mm});
            skLineSegment(sketch, "E166.top", {"start": v(-1388.53, 520.7) * mm, "end": v(-757.77, 520.7) * mm});
            skLineSegment(sketch, "E166.left", {"start": v(-1388.53, 609.6) * mm, "end": v(-1388.53, 520.7) * mm});
            skLineSegment(sketch, "E166.right", {"start": v(-757.77, 609.6) * mm, "end": v(-757.77, 520.7) * mm});
            skSolve(sketch);
        }
        {
            var Q0;
            Q0=qSketchRegion(id+"F44",true);
            var Q1;
            Q1=sQuery(id+"F2.wireOp",VERTEX,"E69.end");
            extrude(context, id + "F45", {"entities" : qUnion([Q0]), "operationType" : NewBodyOperationType.ADD, "endBound" : BoundingType.UP_TO_VERTEX, "depth" : 25.4 * mm, "endBoundEntityVertex" : qUnion([Q1]), "offsetDistance" : 25.4 * mm});
        }
        {
            var Q0;
            Q0=makeQuery(id+"F45.opExtrude","SWEPT_FACE",FACE,{"disambiguationData":[OSD([sQuery(id+"F44.wireOp",EDGE,"E166.bottom")])]});
            var sketch = newSketch(context, id + "F46", { "sketchPlane" : qUnion([Q0])});
            skLineSegment(sketch, "E167.0", {"start": v(304.8, 1375.83) * mm, "end": v(76.2, 1375.83) * mm});
            skLineSegment(sketch, "E167.1", {"start": v(304.8, 770.47) * mm, "end": v(304.8, 1375.83) * mm});
            skLineSegment(sketch, "E167.2", {"start": v(76.2, 770.47) * mm, "end": v(304.8, 770.47) * mm});
            skLineSegment(sketch, "E167.3", {"start": v(76.2, 1375.83) * mm, "end": v(76.2, 770.47) * mm});
            skSolve(sketch);
        }
        {
            var Q0;
            Q0=qSketchRegion(id+"F46",true);
            extrude(context, id + "F47", {"entities" : qUnion([Q0]), "operationType" : NewBodyOperationType.REMOVE, "oppositeDirection" : true, "depth" : 139.7 * mm, "offsetDistance" : 25.4 * mm});
        }
        {
            var Q0;
            Q0=makeQuery(id+"F31.opExtrude","CAP_FACE",FACE,{"disambiguationData":[OSD([sQuery(id+"F30.wireOp",EDGE,"E153.bottom"),sQuery(id+"F30.wireOp",EDGE,"E153.top"),sQuery(id+"F30.wireOp",EDGE,"E153.left"),sQuery(id+"F30.wireOp",EDGE,"E153.right")])],"isStart":true});
            var sketch = newSketch(context, id + "F48", { "sketchPlane" : qUnion([Q0])});
            skLineSegment(sketch, "E168.bottom", {"start": v(-1388.53, 711.2) * mm, "end": v(-757.77, 711.2) * mm});
            skLineSegment(sketch, "E168.top", {"start": v(-1388.53, 800.1) * mm, "end": v(-757.77, 800.1) * mm});
            skLineSegment(sketch, "E168.left", {"start": v(-1388.53, 711.2) * mm, "end": v(-1388.53, 800.1) * mm});
            skLineSegment(sketch, "E168.right", {"start": v(-757.77, 711.2) * mm, "end": v(-757.77, 800.1) * mm});
            skSolve(sketch);
        }
        {
            var Q0;
            Q0=qSketchRegion(id+"F48",true);
            var Q1;
            Q1=sQuery(id+"F2.wireOp",VERTEX,"E69.end");
            extrude(context, id + "F49", {"entities" : qUnion([Q0]), "operationType" : NewBodyOperationType.ADD, "endBound" : BoundingType.UP_TO_VERTEX, "depth" : 25.4 * mm, "endBoundEntityVertex" : qUnion([Q1]), "offsetDistance" : 25.4 * mm});
        }
        {
            var Q0;
            Q0=makeQuery(id+"F49.opExtrude","SWEPT_FACE",FACE,{"disambiguationData":[OSD([sQuery(id+"F48.wireOp",EDGE,"E168.top")])]});
            var sketch = newSketch(context, id + "F50", { "sketchPlane" : qUnion([Q0])});
            skLineSegment(sketch, "E169.0", {"start": v(304.8, 1375.83) * mm, "end": v(76.2, 1375.83) * mm});
            skLineSegment(sketch, "E169.1", {"start": v(304.8, 770.47) * mm, "end": v(304.8, 1375.83) * mm});
            skLineSegment(sketch, "E169.2", {"start": v(76.2, 770.47) * mm, "end": v(304.8, 770.47) * mm});
            skLineSegment(sketch, "E169.3", {"start": v(76.2, 1375.83) * mm, "end": v(76.2, 770.47) * mm});
            skSolve(sketch);
        }
        {
            var Q0;
            Q0=qSketchRegion(id+"F50",true);
            extrude(context, id + "F51", {"entities" : qUnion([Q0]), "operationType" : NewBodyOperationType.REMOVE, "oppositeDirection" : true, "depth" : 139.7 * mm, "offsetDistance" : 25.4 * mm});
        }
        {
            var Q0;
            Q0=makeQuery(id+"F15.opExtrude","CAP_FACE",FACE,{"disambiguationData":[OSD([sQuery(id+"F14.wireOp",EDGE,"E130.bottom"),sQuery(id+"F14.wireOp",EDGE,"E130.top"),sQuery(id+"F14.wireOp",EDGE,"E130.left"),sQuery(id+"F14.wireOp",EDGE,"E130.right")])],"isStart":false});
            var sketch = newSketch(context, id + "F52", { "sketchPlane" : qUnion([Q0])});
            skLineSegment(sketch, "E170.0", {"start": v(0, 1452.03) * mm, "end": v(355.6, 1452.03) * mm});
            skLineSegment(sketch, "E170.1", {"start": v(355.6, 1452.03) * mm, "end": v(355.6, 738.72) * mm});
            skLineSegment(sketch, "E170.2", {"start": v(355.6, 738.72) * mm, "end": v(558.8, 738.72) * mm});
            skLineSegment(sketch, "E170.3", {"start": v(558.8, 738.72) * mm, "end": v(558.8, 0) * mm});
            skLineSegment(sketch, "E170.4", {"start": v(558.8, 0) * mm, "end": v(0, 0) * mm});
            skLineSegment(sketch, "E170.5", {"start": v(0, 0) * mm, "end": v(0, 1452.03) * mm});
            skSolve(sketch);
        }
        {
            var Q0;
            Q0=qSketchRegion(id+"F52",true);
            extrude(context, id + "F53", {"entities" : qUnion([Q0]), "depth" : 19.05 * mm, "offsetDistance" : 25.4 * mm});
        }
        {
            var Q0;
            Q0=makeQuery(id+"F53.opExtrude","CAP_FACE",FACE,{"disambiguationData":[OSD([sQuery(id+"F52.wireOp",EDGE,"E170.0"),sQuery(id+"F52.wireOp",EDGE,"E170.1"),sQuery(id+"F52.wireOp",EDGE,"E170.2"),sQuery(id+"F52.wireOp",EDGE,"E170.3"),sQuery(id+"F52.wireOp",EDGE,"E170.4"),sQuery(id+"F52.wireOp",EDGE,"E170.5")])],"isStart":false});
            var sketch = newSketch(context, id + "F54", { "sketchPlane" : qUnion([Q0])});
            skLineSegment(sketch, "E171.bottom", {"start": v(0, 0) * mm, "end": v(19.05, 0) * mm});
            skLineSegment(sketch, "E171.top", {"start": v(0, 1452.03) * mm, "end": v(19.05, 1452.03) * mm});
            skLineSegment(sketch, "E171.left", {"start": v(0, 0) * mm, "end": v(0, 1452.03) * mm});
            skLineSegment(sketch, "E171.right", {"start": v(19.05, 0) * mm, "end": v(19.05, 1452.03) * mm});
            skSolve(sketch);
        }
        {
            var Q0;
            Q0=qSketchRegion(id+"F54",true);
            extrude(context, id + "F55", {"entities" : qUnion([Q0]), "depth" : 76.2 * mm, "offsetDistance" : 25.4 * mm});
        }
        {
            var Q0;
            Q0=makeQuery(id+"F53.opExtrude","SWEPT_EDGE",EDGE,{"disambiguationData":[OSD([sQuery(id+"F52.wireOp",EDGE,"E170.2"),sQuery(id+"F52.wireOp",EDGE,"E170.3")])]});
            var Q1;
            Q1=makeQuery(id+"F53.opExtrude","SWEPT_EDGE",EDGE,{"disambiguationData":[OSD([sQuery(id+"F52.wireOp",EDGE,"E170.0"),sQuery(id+"F52.wireOp",EDGE,"E170.1")])]});
            var Q2;
            Q2=makeQuery(id+"F55.opExtrude","CAP_EDGE",EDGE,{"disambiguationData":[OSD([sQuery(id+"F54.wireOp",EDGE,"E171.top")])],"isStart":false});
            var Q3;
            Q3=makeQuery(id+"F53.opExtrude","SWEPT_EDGE",EDGE,{"disambiguationData":[OSD([sQuery(id+"F52.wireOp",EDGE,"E170.1"),sQuery(id+"F52.wireOp",EDGE,"E170.2")])]});
            fillet(context, id + "F56", {"entities" : qUnion([Q0, Q1, Q2, Q3]), "radius" : 25.4 * mm, "tangentPropagation" : true, "allowEdgeOverflow" : false});
        }
        {
            var Q0;
            Q0=makeQuery(id+"F53.opExtrude","CAP_EDGE",EDGE,{"disambiguationData":[OSD([sQuery(id+"F52.wireOp",EDGE,"E170.3")])],"isStart":true});
            var Q1;
            Q1=makeQuery(id+"F55.opExtrude","SWEPT_EDGE",EDGE,{"disambiguationData":[OSD([sQuery(id+"F52.wireOp",EDGE,"E170.0"),sQuery(id+"F54.wireOp",EDGE,"E171.top"),sQuery(id+"F54.wireOp",EDGE,"E171.right")])]});
            chamfer(context, id + "F57", {"entities" : qUnion([Q0, Q1]), "width" : 6.35 * mm, "tangentPropagation" : true});
        }
    });
